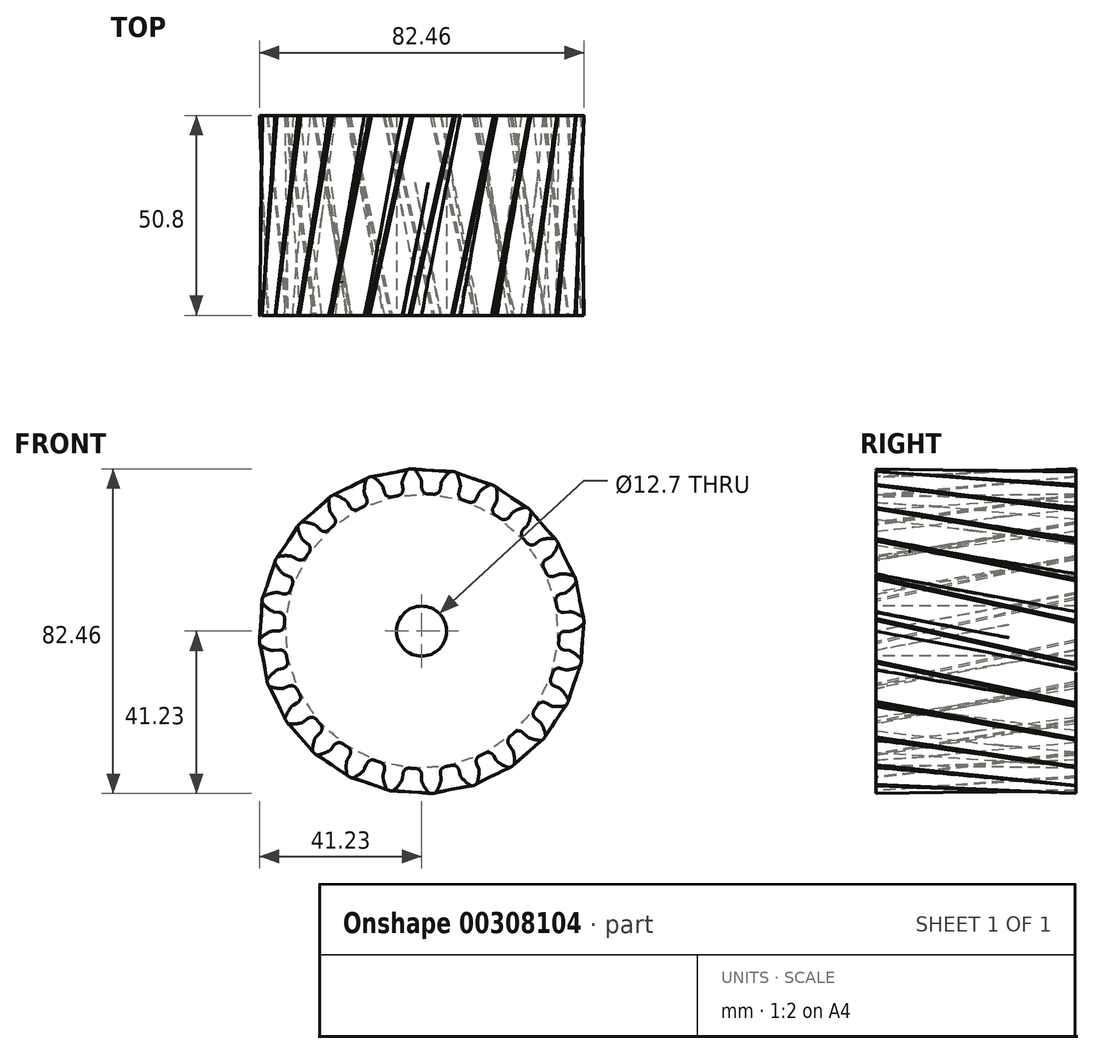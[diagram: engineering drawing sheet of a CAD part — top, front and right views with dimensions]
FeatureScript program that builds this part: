
annotation { "Feature Type Name" : "Feature", "Feature Type Description" : "" }
export const myFeature = defineFeature(function(context is Context, id is Id, definition is map)
    precondition{}
    {
        {
            var Q0;
            Q0=qCreatedBy(makeId("Front.planeOp"),FACE);
            var sketch = newSketch(context, id + "F0", { "sketchPlane" : qUnion([Q0])});
            skArc(sketch, "E0", {"start": v(-6.07, 34.4) * mm, "mid": v(-6.81, 34.25) * mm, "end": v(-7.56, 34.1) * mm});
            skArc(sketch, "E1.trimOffspring", {"start": v(-0.12, 38.41) * mm, "mid": v(-0.85, 39.8) * mm, "end": v(-1.8, 41.06) * mm});
            skLineSegment(sketch, "E2", {"start": v(-2.18, 41.23) * mm, "end": v(-2.7, 41.23) * mm});
            skLineSegment(sketch, "E3", {"start": v(0, 37.8) * mm, "end": v(0, 36.48) * mm});
            skLineSegment(sketch, "E4.MirrorCS", {"start": v(-3.22, 41.16) * mm, "end": v(-2.7, 41.23) * mm});
            skArc(sketch, "E5.MirrorCS", {"start": v(-4.9, 38.1) * mm, "mid": v(-4.35, 39.58) * mm, "end": v(-3.57, 40.95) * mm});
            skLineSegment(sketch, "E6.MirrorCS", {"start": v(-4.94, 37.47) * mm, "end": v(-4.77, 36.16) * mm});
            skPoint(sketch, "E7.visualSharp", {"position": v(-3.44, 41.13) * mm});
            skArc(sketch, "E7.filletArc", {"start": v(-3.22, 41.16) * mm, "mid": v(-3.41, 41.1) * mm, "end": v(-3.57, 40.95) * mm});
            skPoint(sketch, "E8.visualSharp", {"position": v(-1.96, 41.23) * mm});
            skArc(sketch, "E8.filletArc", {"start": v(-1.8, 41.06) * mm, "mid": v(-1.98, 41.18) * mm, "end": v(-2.18, 41.23) * mm});
            skPoint(sketch, "E9.visualSharp", {"position": v(-4.98, 37.77) * mm});
            skArc(sketch, "E9.filletArc", {"start": v(-4.9, 38.1) * mm, "mid": v(-4.95, 37.79) * mm, "end": v(-4.94, 37.47) * mm});
            skPoint(sketch, "E10.visualSharp", {"position": v(0, 38.1) * mm});
            skArc(sketch, "E10.filletArc", {"start": v(0, 37.8) * mm, "mid": v(-0.02, 38.1) * mm, "end": v(-0.12, 38.41) * mm});
            skPoint(sketch, "E11.visualSharp", {"position": v(0, 34.92) * mm});
            skArc(sketch, "E11.filletArc", {"start": v(0, 36.48) * mm, "mid": v(0.45, 35.38) * mm, "end": v(1.53, 34.9) * mm});
            skPoint(sketch, "E12.visualSharp", {"position": v(-4.57, 34.63) * mm});
            skArc(sketch, "E12.filletArc", {"start": v(-6.07, 34.4) * mm, "mid": v(-5.06, 35.02) * mm, "end": v(-4.77, 36.16) * mm});
            skLineSegment(sketch, "E13.1.0", {"start": v(-14.47, 34.91) * mm, "end": v(-13.97, 33.7) * mm});
            skArc(sketch, "E13.1.1", {"start": v(-14.76, 31.65) * mm, "mid": v(-13.95, 32.51) * mm, "end": v(-13.97, 33.7) * mm});
            skLineSegment(sketch, "E13.1.2", {"start": v(-9.77, 36.5) * mm, "end": v(-9.43, 35.24) * mm});
            skArc(sketch, "E13.1.3", {"start": v(-9.43, 35.24) * mm, "mid": v(-8.72, 34.3) * mm, "end": v(-7.56, 34.1) * mm});
            skArc(sketch, "E13.1.4", {"start": v(-14.6, 35.53) * mm, "mid": v(-14.56, 35.22) * mm, "end": v(-14.47, 34.91) * mm});
            skArc(sketch, "E13.1.5", {"start": v(-14.6, 35.53) * mm, "mid": v(-14.45, 37.1) * mm, "end": v(-14.04, 38.63) * mm});
            skArc(sketch, "E13.1.6", {"start": v(-13.76, 38.93) * mm, "mid": v(-13.93, 38.8) * mm, "end": v(-14.04, 38.63) * mm});
            skLineSegment(sketch, "E13.1.7", {"start": v(-13.76, 38.93) * mm, "end": v(-13.28, 39.12) * mm});
            skLineSegment(sketch, "E13.1.8", {"start": v(-12.78, 39.26) * mm, "end": v(-13.28, 39.12) * mm});
            skArc(sketch, "E13.1.9", {"start": v(-12.37, 39.2) * mm, "mid": v(-12.57, 39.27) * mm, "end": v(-12.78, 39.26) * mm});
            skArc(sketch, "E13.1.10", {"start": v(-10.06, 37.07) * mm, "mid": v(-11.13, 38.23) * mm, "end": v(-12.37, 39.2) * mm});
            skArc(sketch, "E13.1.11", {"start": v(-9.77, 36.5) * mm, "mid": v(-9.89, 36.8) * mm, "end": v(-10.06, 37.07) * mm});
            skLineSegment(sketch, "E13.2.0", {"start": v(-23.01, 29.98) * mm, "end": v(-22.21, 28.93) * mm});
            skArc(sketch, "E13.2.1", {"start": v(-22.45, 26.75) * mm, "mid": v(-21.9, 27.8) * mm, "end": v(-22.21, 28.93) * mm});
            skLineSegment(sketch, "E13.2.2", {"start": v(-18.89, 32.73) * mm, "end": v(-18.23, 31.6) * mm});
            skArc(sketch, "E13.2.3", {"start": v(-18.23, 31.6) * mm, "mid": v(-17.3, 30.86) * mm, "end": v(-16.12, 30.98) * mm});
            skArc(sketch, "E13.2.4", {"start": v(-23.3, 30.55) * mm, "mid": v(-23.18, 30.25) * mm, "end": v(-23.01, 29.98) * mm});
            skArc(sketch, "E13.2.5", {"start": v(-23.3, 30.55) * mm, "mid": v(-23.56, 32.1) * mm, "end": v(-23.56, 33.68) * mm});
            skArc(sketch, "E13.2.6", {"start": v(-23.36, 34.04) * mm, "mid": v(-23.5, 33.88) * mm, "end": v(-23.56, 33.68) * mm});
            skLineSegment(sketch, "E13.2.7", {"start": v(-23.36, 34.04) * mm, "end": v(-22.95, 34.35) * mm});
            skLineSegment(sketch, "E13.2.8", {"start": v(-22.5, 34.61) * mm, "end": v(-22.95, 34.35) * mm});
            skArc(sketch, "E13.2.9", {"start": v(-22.1, 34.66) * mm, "mid": v(-22.3, 34.68) * mm, "end": v(-22.5, 34.61) * mm});
            skArc(sketch, "E13.2.10", {"start": v(-19.3, 33.2) * mm, "mid": v(-20.64, 34.05) * mm, "end": v(-22.1, 34.66) * mm});
            skArc(sketch, "E13.2.11", {"start": v(-18.89, 32.73) * mm, "mid": v(-19.07, 33) * mm, "end": v(-19.3, 33.2) * mm});
            skLineSegment(sketch, "E14.2.3.0", {"start": v(-29.99, 23) * mm, "end": v(-28.94, 22.2) * mm});
            skArc(sketch, "E14.3.3.0", {"start": v(-28.61, 20.03) * mm, "mid": v(-28.34, 21.18) * mm, "end": v(-28.94, 22.2) * mm});
            skLineSegment(sketch, "E14.7.3.0", {"start": v(-26.72, 26.73) * mm, "end": v(-25.79, 25.8) * mm});
            skArc(sketch, "E14.10.3.0", {"start": v(-25.79, 25.8) * mm, "mid": v(-24.7, 25.34) * mm, "end": v(-23.6, 25.75) * mm});
            skArc(sketch, "E14.14.3.0", {"start": v(-30.4, 23.48) * mm, "mid": v(-30.22, 23.22) * mm, "end": v(-29.99, 23) * mm});
            skArc(sketch, "E14.18.3.0", {"start": v(-30.4, 23.48) * mm, "mid": v(-31.06, 24.9) * mm, "end": v(-31.48, 26.43) * mm});
            skArc(sketch, "E14.22.3.0", {"start": v(-31.38, 26.83) * mm, "mid": v(-31.47, 26.64) * mm, "end": v(-31.48, 26.43) * mm});
            skLineSegment(sketch, "E14.26.3.0", {"start": v(-31.38, 26.83) * mm, "end": v(-31.06, 27.24) * mm});
            skLineSegment(sketch, "E14.29.3.0", {"start": v(-30.7, 27.6) * mm, "end": v(-31.06, 27.24) * mm});
            skArc(sketch, "E14.32.3.0", {"start": v(-30.31, 27.76) * mm, "mid": v(-30.52, 27.72) * mm, "end": v(-30.7, 27.6) * mm});
            skArc(sketch, "E14.36.3.0", {"start": v(-27.25, 27.08) * mm, "mid": v(-28.75, 27.54) * mm, "end": v(-30.31, 27.76) * mm});
            skArc(sketch, "E14.40.3.0", {"start": v(-26.72, 26.73) * mm, "mid": v(-26.96, 26.93) * mm, "end": v(-27.25, 27.08) * mm});
            skLineSegment(sketch, "E14.2.4.0", {"start": v(-34.92, 14.45) * mm, "end": v(-33.7, 13.95) * mm});
            skArc(sketch, "E14.3.4.0", {"start": v(-32.82, 11.94) * mm, "mid": v(-32.86, 13.12) * mm, "end": v(-33.7, 13.95) * mm});
            skLineSegment(sketch, "E14.7.4.0", {"start": v(-32.72, 18.9) * mm, "end": v(-31.59, 18.25) * mm});
            skArc(sketch, "E14.10.4.0", {"start": v(-31.59, 18.25) * mm, "mid": v(-30.42, 18.08) * mm, "end": v(-29.45, 18.77) * mm});
            skArc(sketch, "E14.14.4.0", {"start": v(-35.44, 14.8) * mm, "mid": v(-35.2, 14.6) * mm, "end": v(-34.92, 14.45) * mm});
            skArc(sketch, "E14.18.4.0", {"start": v(-35.44, 14.8) * mm, "mid": v(-36.45, 16.02) * mm, "end": v(-37.24, 17.38) * mm});
            skArc(sketch, "E14.22.4.0", {"start": v(-37.25, 17.8) * mm, "mid": v(-37.3, 17.59) * mm, "end": v(-37.24, 17.38) * mm});
            skLineSegment(sketch, "E14.26.4.0", {"start": v(-37.25, 17.8) * mm, "end": v(-37.06, 18.27) * mm});
            skLineSegment(sketch, "E14.29.4.0", {"start": v(-36.8, 18.72) * mm, "end": v(-37.06, 18.27) * mm});
            skArc(sketch, "E14.32.4.0", {"start": v(-36.46, 18.96) * mm, "mid": v(-36.66, 18.88) * mm, "end": v(-36.8, 18.72) * mm});
            skArc(sketch, "E14.36.4.0", {"start": v(-33.33, 19.1) * mm, "mid": v(-34.9, 19.16) * mm, "end": v(-36.46, 18.96) * mm});
            skArc(sketch, "E14.40.4.0", {"start": v(-32.72, 18.9) * mm, "mid": v(-33.01, 19.03) * mm, "end": v(-33.33, 19.1) * mm});
            skLineSegment(sketch, "E14.2.5.0", {"start": v(-37.47, 4.92) * mm, "end": v(-36.17, 4.75) * mm});
            skArc(sketch, "E14.3.5.0", {"start": v(-34.8, 3.04) * mm, "mid": v(-35.14, 4.17) * mm, "end": v(-36.17, 4.75) * mm});
            skLineSegment(sketch, "E14.7.5.0", {"start": v(-36.5, 9.79) * mm, "end": v(-35.23, 9.45) * mm});
            skArc(sketch, "E14.10.5.0", {"start": v(-35.23, 9.45) * mm, "mid": v(-34.06, 9.6) * mm, "end": v(-33.3, 10.5) * mm});
            skArc(sketch, "E14.14.5.0", {"start": v(-38.07, 5.13) * mm, "mid": v(-37.78, 5) * mm, "end": v(-37.47, 4.92) * mm});
            skArc(sketch, "E14.18.5.0", {"start": v(-38.07, 5.13) * mm, "mid": v(-39.36, 6.04) * mm, "end": v(-40.47, 7.15) * mm});
            skArc(sketch, "E14.22.5.0", {"start": v(-40.6, 7.55) * mm, "mid": v(-40.57, 7.34) * mm, "end": v(-40.47, 7.15) * mm});
            skLineSegment(sketch, "E14.26.5.0", {"start": v(-40.6, 7.55) * mm, "end": v(-40.52, 8.06) * mm});
            skLineSegment(sketch, "E14.29.5.0", {"start": v(-40.39, 8.56) * mm, "end": v(-40.52, 8.06) * mm});
            skArc(sketch, "E14.32.5.0", {"start": v(-40.13, 8.88) * mm, "mid": v(-40.3, 8.75) * mm, "end": v(-40.39, 8.56) * mm});
            skArc(sketch, "E14.36.5.0", {"start": v(-37.13, 9.83) * mm, "mid": v(-38.67, 9.48) * mm, "end": v(-40.13, 8.88) * mm});
            skArc(sketch, "E14.40.5.0", {"start": v(-36.5, 9.79) * mm, "mid": v(-36.82, 9.84) * mm, "end": v(-37.13, 9.83) * mm});
            skLineSegment(sketch, "E14.2.6.0", {"start": v(-37.47, -4.94) * mm, "end": v(-36.16, -4.77) * mm});
            skArc(sketch, "E14.3.6.0", {"start": v(-34.4, -6.07) * mm, "mid": v(-35.02, -5.06) * mm, "end": v(-36.16, -4.77) * mm});
            skLineSegment(sketch, "E14.7.6.0", {"start": v(-37.8, 0) * mm, "end": v(-36.48, 0) * mm});
            skArc(sketch, "E14.10.6.0", {"start": v(-36.48, 0) * mm, "mid": v(-35.38, 0.45) * mm, "end": v(-34.9, 1.53) * mm});
            skArc(sketch, "E14.14.6.0", {"start": v(-38.1, -4.9) * mm, "mid": v(-37.79, -4.95) * mm, "end": v(-37.47, -4.94) * mm});
            skArc(sketch, "E14.18.6.0", {"start": v(-38.1, -4.9) * mm, "mid": v(-39.58, -4.35) * mm, "end": v(-40.95, -3.57) * mm});
            skArc(sketch, "E14.22.6.0", {"start": v(-41.16, -3.22) * mm, "mid": v(-41.1, -3.41) * mm, "end": v(-40.95, -3.57) * mm});
            skLineSegment(sketch, "E14.26.6.0", {"start": v(-41.16, -3.22) * mm, "end": v(-41.23, -2.7) * mm});
            skLineSegment(sketch, "E14.29.6.0", {"start": v(-41.23, -2.18) * mm, "end": v(-41.23, -2.7) * mm});
            skArc(sketch, "E14.32.6.0", {"start": v(-41.06, -1.8) * mm, "mid": v(-41.18, -1.98) * mm, "end": v(-41.23, -2.18) * mm});
            skArc(sketch, "E14.36.6.0", {"start": v(-38.41, -0.12) * mm, "mid": v(-39.8, -0.85) * mm, "end": v(-41.06, -1.8) * mm});
            skArc(sketch, "E14.40.6.0", {"start": v(-37.8, 0) * mm, "mid": v(-38.1, -0.02) * mm, "end": v(-38.41, -0.12) * mm});
            skLineSegment(sketch, "E14.2.7.0", {"start": v(-34.91, -14.47) * mm, "end": v(-33.7, -13.97) * mm});
            skArc(sketch, "E14.3.7.0", {"start": v(-31.65, -14.76) * mm, "mid": v(-32.51, -13.95) * mm, "end": v(-33.7, -13.97) * mm});
            skLineSegment(sketch, "E14.7.7.0", {"start": v(-36.5, -9.77) * mm, "end": v(-35.24, -9.43) * mm});
            skArc(sketch, "E14.10.7.0", {"start": v(-35.24, -9.43) * mm, "mid": v(-34.3, -8.72) * mm, "end": v(-34.1, -7.56) * mm});
            skArc(sketch, "E14.14.7.0", {"start": v(-35.53, -14.6) * mm, "mid": v(-35.22, -14.56) * mm, "end": v(-34.91, -14.47) * mm});
            skArc(sketch, "E14.18.7.0", {"start": v(-35.53, -14.6) * mm, "mid": v(-37.1, -14.45) * mm, "end": v(-38.63, -14.04) * mm});
            skArc(sketch, "E14.22.7.0", {"start": v(-38.93, -13.76) * mm, "mid": v(-38.8, -13.93) * mm, "end": v(-38.63, -14.04) * mm});
            skLineSegment(sketch, "E14.26.7.0", {"start": v(-38.93, -13.76) * mm, "end": v(-39.12, -13.28) * mm});
            skLineSegment(sketch, "E14.29.7.0", {"start": v(-39.26, -12.78) * mm, "end": v(-39.12, -13.28) * mm});
            skArc(sketch, "E14.32.7.0", {"start": v(-39.2, -12.37) * mm, "mid": v(-39.27, -12.57) * mm, "end": v(-39.26, -12.78) * mm});
            skArc(sketch, "E14.36.7.0", {"start": v(-37.07, -10.06) * mm, "mid": v(-38.23, -11.13) * mm, "end": v(-39.2, -12.37) * mm});
            skArc(sketch, "E14.40.7.0", {"start": v(-36.5, -9.77) * mm, "mid": v(-36.8, -9.89) * mm, "end": v(-37.07, -10.06) * mm});
            skLineSegment(sketch, "E14.2.8.0", {"start": v(-29.98, -23.01) * mm, "end": v(-28.93, -22.21) * mm});
            skArc(sketch, "E14.3.8.0", {"start": v(-26.75, -22.45) * mm, "mid": v(-27.8, -21.9) * mm, "end": v(-28.93, -22.21) * mm});
            skLineSegment(sketch, "E14.7.8.0", {"start": v(-32.73, -18.89) * mm, "end": v(-31.6, -18.23) * mm});
            skArc(sketch, "E14.10.8.0", {"start": v(-31.6, -18.23) * mm, "mid": v(-30.86, -17.3) * mm, "end": v(-30.98, -16.12) * mm});
            skArc(sketch, "E14.14.8.0", {"start": v(-30.55, -23.3) * mm, "mid": v(-30.25, -23.18) * mm, "end": v(-29.98, -23.01) * mm});
            skArc(sketch, "E14.18.8.0", {"start": v(-30.55, -23.3) * mm, "mid": v(-32.1, -23.56) * mm, "end": v(-33.68, -23.56) * mm});
            skArc(sketch, "E14.22.8.0", {"start": v(-34.04, -23.36) * mm, "mid": v(-33.88, -23.5) * mm, "end": v(-33.68, -23.56) * mm});
            skLineSegment(sketch, "E14.26.8.0", {"start": v(-34.04, -23.36) * mm, "end": v(-34.35, -22.95) * mm});
            skLineSegment(sketch, "E14.29.8.0", {"start": v(-34.61, -22.5) * mm, "end": v(-34.35, -22.95) * mm});
            skArc(sketch, "E14.32.8.0", {"start": v(-34.66, -22.1) * mm, "mid": v(-34.68, -22.3) * mm, "end": v(-34.61, -22.5) * mm});
            skArc(sketch, "E14.36.8.0", {"start": v(-33.2, -19.3) * mm, "mid": v(-34.05, -20.64) * mm, "end": v(-34.66, -22.1) * mm});
            skArc(sketch, "E14.40.8.0", {"start": v(-32.73, -18.89) * mm, "mid": v(-33, -19.07) * mm, "end": v(-33.2, -19.3) * mm});
            skLineSegment(sketch, "E14.2.9.0", {"start": v(-23, -29.99) * mm, "end": v(-22.2, -28.94) * mm});
            skArc(sketch, "E14.3.9.0", {"start": v(-20.03, -28.61) * mm, "mid": v(-21.18, -28.34) * mm, "end": v(-22.2, -28.94) * mm});
            skLineSegment(sketch, "E14.7.9.0", {"start": v(-26.73, -26.72) * mm, "end": v(-25.8, -25.79) * mm});
            skArc(sketch, "E14.10.9.0", {"start": v(-25.8, -25.79) * mm, "mid": v(-25.34, -24.7) * mm, "end": v(-25.75, -23.6) * mm});
            skArc(sketch, "E14.14.9.0", {"start": v(-23.48, -30.4) * mm, "mid": v(-23.22, -30.22) * mm, "end": v(-23, -29.99) * mm});
            skArc(sketch, "E14.18.9.0", {"start": v(-23.48, -30.4) * mm, "mid": v(-24.9, -31.06) * mm, "end": v(-26.43, -31.48) * mm});
            skArc(sketch, "E14.22.9.0", {"start": v(-26.83, -31.38) * mm, "mid": v(-26.64, -31.47) * mm, "end": v(-26.43, -31.48) * mm});
            skLineSegment(sketch, "E14.26.9.0", {"start": v(-26.83, -31.38) * mm, "end": v(-27.24, -31.06) * mm});
            skLineSegment(sketch, "E14.29.9.0", {"start": v(-27.6, -30.7) * mm, "end": v(-27.24, -31.06) * mm});
            skArc(sketch, "E14.32.9.0", {"start": v(-27.76, -30.31) * mm, "mid": v(-27.72, -30.52) * mm, "end": v(-27.6, -30.7) * mm});
            skArc(sketch, "E14.36.9.0", {"start": v(-27.08, -27.25) * mm, "mid": v(-27.54, -28.75) * mm, "end": v(-27.76, -30.31) * mm});
            skArc(sketch, "E14.40.9.0", {"start": v(-26.73, -26.72) * mm, "mid": v(-26.93, -26.96) * mm, "end": v(-27.08, -27.25) * mm});
            skLineSegment(sketch, "E14.2.10.0", {"start": v(-14.45, -34.92) * mm, "end": v(-13.95, -33.7) * mm});
            skArc(sketch, "E14.3.10.0", {"start": v(-11.94, -32.82) * mm, "mid": v(-13.12, -32.86) * mm, "end": v(-13.95, -33.7) * mm});
            skLineSegment(sketch, "E14.7.10.0", {"start": v(-18.9, -32.72) * mm, "end": v(-18.25, -31.59) * mm});
            skArc(sketch, "E14.10.10.0", {"start": v(-18.25, -31.59) * mm, "mid": v(-18.08, -30.42) * mm, "end": v(-18.77, -29.45) * mm});
            skArc(sketch, "E14.14.10.0", {"start": v(-14.8, -35.44) * mm, "mid": v(-14.6, -35.2) * mm, "end": v(-14.45, -34.92) * mm});
            skArc(sketch, "E14.18.10.0", {"start": v(-14.8, -35.44) * mm, "mid": v(-16.02, -36.45) * mm, "end": v(-17.38, -37.24) * mm});
            skArc(sketch, "E14.22.10.0", {"start": v(-17.8, -37.25) * mm, "mid": v(-17.59, -37.3) * mm, "end": v(-17.38, -37.24) * mm});
            skLineSegment(sketch, "E14.26.10.0", {"start": v(-17.8, -37.25) * mm, "end": v(-18.27, -37.06) * mm});
            skLineSegment(sketch, "E14.29.10.0", {"start": v(-18.72, -36.8) * mm, "end": v(-18.27, -37.06) * mm});
            skArc(sketch, "E14.32.10.0", {"start": v(-18.96, -36.46) * mm, "mid": v(-18.88, -36.66) * mm, "end": v(-18.72, -36.8) * mm});
            skArc(sketch, "E14.36.10.0", {"start": v(-19.1, -33.33) * mm, "mid": v(-19.16, -34.9) * mm, "end": v(-18.96, -36.46) * mm});
            skArc(sketch, "E14.40.10.0", {"start": v(-18.9, -32.72) * mm, "mid": v(-19.03, -33.01) * mm, "end": v(-19.1, -33.33) * mm});
            skLineSegment(sketch, "E14.2.11.0", {"start": v(-4.92, -37.47) * mm, "end": v(-4.75, -36.17) * mm});
            skArc(sketch, "E14.3.11.0", {"start": v(-3.04, -34.8) * mm, "mid": v(-4.17, -35.14) * mm, "end": v(-4.75, -36.17) * mm});
            skLineSegment(sketch, "E14.7.11.0", {"start": v(-9.79, -36.5) * mm, "end": v(-9.45, -35.23) * mm});
            skArc(sketch, "E14.10.11.0", {"start": v(-9.45, -35.23) * mm, "mid": v(-9.6, -34.06) * mm, "end": v(-10.5, -33.3) * mm});
            skArc(sketch, "E14.14.11.0", {"start": v(-5.13, -38.07) * mm, "mid": v(-5, -37.78) * mm, "end": v(-4.92, -37.47) * mm});
            skArc(sketch, "E14.18.11.0", {"start": v(-5.13, -38.07) * mm, "mid": v(-6.04, -39.36) * mm, "end": v(-7.15, -40.47) * mm});
            skArc(sketch, "E14.22.11.0", {"start": v(-7.55, -40.6) * mm, "mid": v(-7.34, -40.57) * mm, "end": v(-7.15, -40.47) * mm});
            skLineSegment(sketch, "E14.26.11.0", {"start": v(-7.55, -40.6) * mm, "end": v(-8.06, -40.52) * mm});
            skLineSegment(sketch, "E14.29.11.0", {"start": v(-8.56, -40.39) * mm, "end": v(-8.06, -40.52) * mm});
            skArc(sketch, "E14.32.11.0", {"start": v(-8.88, -40.13) * mm, "mid": v(-8.75, -40.3) * mm, "end": v(-8.56, -40.39) * mm});
            skArc(sketch, "E14.36.11.0", {"start": v(-9.83, -37.13) * mm, "mid": v(-9.48, -38.67) * mm, "end": v(-8.88, -40.13) * mm});
            skArc(sketch, "E14.40.11.0", {"start": v(-9.79, -36.5) * mm, "mid": v(-9.84, -36.82) * mm, "end": v(-9.83, -37.13) * mm});
            skLineSegment(sketch, "E14.2.12.0", {"start": v(4.94, -37.47) * mm, "end": v(4.77, -36.16) * mm});
            skArc(sketch, "E14.3.12.0", {"start": v(6.07, -34.4) * mm, "mid": v(5.06, -35.02) * mm, "end": v(4.77, -36.16) * mm});
            skLineSegment(sketch, "E14.7.12.0", {"start": v(0, -37.8) * mm, "end": v(0, -36.48) * mm});
            skArc(sketch, "E14.10.12.0", {"start": v(0, -36.48) * mm, "mid": v(-0.45, -35.38) * mm, "end": v(-1.53, -34.9) * mm});
            skArc(sketch, "E14.14.12.0", {"start": v(4.9, -38.1) * mm, "mid": v(4.95, -37.79) * mm, "end": v(4.94, -37.47) * mm});
            skArc(sketch, "E14.18.12.0", {"start": v(4.9, -38.1) * mm, "mid": v(4.35, -39.58) * mm, "end": v(3.57, -40.95) * mm});
            skArc(sketch, "E14.22.12.0", {"start": v(3.22, -41.16) * mm, "mid": v(3.41, -41.1) * mm, "end": v(3.57, -40.95) * mm});
            skLineSegment(sketch, "E14.26.12.0", {"start": v(3.22, -41.16) * mm, "end": v(2.7, -41.23) * mm});
            skLineSegment(sketch, "E14.29.12.0", {"start": v(2.18, -41.23) * mm, "end": v(2.7, -41.23) * mm});
            skArc(sketch, "E14.32.12.0", {"start": v(1.8, -41.06) * mm, "mid": v(1.98, -41.18) * mm, "end": v(2.18, -41.23) * mm});
            skArc(sketch, "E14.36.12.0", {"start": v(0.12, -38.41) * mm, "mid": v(0.85, -39.8) * mm, "end": v(1.8, -41.06) * mm});
            skArc(sketch, "E14.40.12.0", {"start": v(0, -37.8) * mm, "mid": v(0.02, -38.1) * mm, "end": v(0.12, -38.41) * mm});
            skLineSegment(sketch, "E14.2.13.0", {"start": v(14.47, -34.91) * mm, "end": v(13.97, -33.7) * mm});
            skArc(sketch, "E14.3.13.0", {"start": v(14.76, -31.65) * mm, "mid": v(13.95, -32.51) * mm, "end": v(13.97, -33.7) * mm});
            skLineSegment(sketch, "E14.7.13.0", {"start": v(9.77, -36.5) * mm, "end": v(9.43, -35.24) * mm});
            skArc(sketch, "E14.10.13.0", {"start": v(9.43, -35.24) * mm, "mid": v(8.72, -34.3) * mm, "end": v(7.56, -34.1) * mm});
            skArc(sketch, "E14.14.13.0", {"start": v(14.6, -35.53) * mm, "mid": v(14.56, -35.22) * mm, "end": v(14.47, -34.91) * mm});
            skArc(sketch, "E14.18.13.0", {"start": v(14.6, -35.53) * mm, "mid": v(14.45, -37.1) * mm, "end": v(14.04, -38.63) * mm});
            skArc(sketch, "E14.22.13.0", {"start": v(13.76, -38.93) * mm, "mid": v(13.93, -38.8) * mm, "end": v(14.04, -38.63) * mm});
            skLineSegment(sketch, "E14.26.13.0", {"start": v(13.76, -38.93) * mm, "end": v(13.28, -39.12) * mm});
            skLineSegment(sketch, "E14.29.13.0", {"start": v(12.78, -39.26) * mm, "end": v(13.28, -39.12) * mm});
            skArc(sketch, "E14.32.13.0", {"start": v(12.37, -39.2) * mm, "mid": v(12.57, -39.27) * mm, "end": v(12.78, -39.26) * mm});
            skArc(sketch, "E14.36.13.0", {"start": v(10.06, -37.07) * mm, "mid": v(11.13, -38.23) * mm, "end": v(12.37, -39.2) * mm});
            skArc(sketch, "E14.40.13.0", {"start": v(9.77, -36.5) * mm, "mid": v(9.89, -36.8) * mm, "end": v(10.06, -37.07) * mm});
            skLineSegment(sketch, "E14.2.14.0", {"start": v(23.01, -29.98) * mm, "end": v(22.21, -28.93) * mm});
            skArc(sketch, "E14.3.14.0", {"start": v(22.45, -26.75) * mm, "mid": v(21.9, -27.8) * mm, "end": v(22.21, -28.93) * mm});
            skLineSegment(sketch, "E14.7.14.0", {"start": v(18.89, -32.73) * mm, "end": v(18.23, -31.6) * mm});
            skArc(sketch, "E14.10.14.0", {"start": v(18.23, -31.6) * mm, "mid": v(17.3, -30.86) * mm, "end": v(16.12, -30.98) * mm});
            skArc(sketch, "E14.14.14.0", {"start": v(23.3, -30.55) * mm, "mid": v(23.18, -30.25) * mm, "end": v(23.01, -29.98) * mm});
            skArc(sketch, "E14.18.14.0", {"start": v(23.3, -30.55) * mm, "mid": v(23.56, -32.1) * mm, "end": v(23.56, -33.68) * mm});
            skArc(sketch, "E14.22.14.0", {"start": v(23.36, -34.04) * mm, "mid": v(23.5, -33.88) * mm, "end": v(23.56, -33.68) * mm});
            skLineSegment(sketch, "E14.26.14.0", {"start": v(23.36, -34.04) * mm, "end": v(22.95, -34.35) * mm});
            skLineSegment(sketch, "E14.29.14.0", {"start": v(22.5, -34.61) * mm, "end": v(22.95, -34.35) * mm});
            skArc(sketch, "E14.32.14.0", {"start": v(22.1, -34.66) * mm, "mid": v(22.3, -34.68) * mm, "end": v(22.5, -34.61) * mm});
            skArc(sketch, "E14.36.14.0", {"start": v(19.3, -33.2) * mm, "mid": v(20.64, -34.05) * mm, "end": v(22.1, -34.66) * mm});
            skArc(sketch, "E14.40.14.0", {"start": v(18.89, -32.73) * mm, "mid": v(19.07, -33) * mm, "end": v(19.3, -33.2) * mm});
            skLineSegment(sketch, "E14.2.15.0", {"start": v(29.99, -23) * mm, "end": v(28.94, -22.2) * mm});
            skArc(sketch, "E14.3.15.0", {"start": v(28.61, -20.03) * mm, "mid": v(28.34, -21.18) * mm, "end": v(28.94, -22.2) * mm});
            skLineSegment(sketch, "E14.7.15.0", {"start": v(26.72, -26.73) * mm, "end": v(25.79, -25.8) * mm});
            skArc(sketch, "E14.10.15.0", {"start": v(25.79, -25.8) * mm, "mid": v(24.7, -25.34) * mm, "end": v(23.6, -25.75) * mm});
            skArc(sketch, "E14.14.15.0", {"start": v(30.4, -23.48) * mm, "mid": v(30.22, -23.22) * mm, "end": v(29.99, -23) * mm});
            skArc(sketch, "E14.18.15.0", {"start": v(30.4, -23.48) * mm, "mid": v(31.06, -24.9) * mm, "end": v(31.48, -26.43) * mm});
            skArc(sketch, "E14.22.15.0", {"start": v(31.38, -26.83) * mm, "mid": v(31.47, -26.64) * mm, "end": v(31.48, -26.43) * mm});
            skLineSegment(sketch, "E14.26.15.0", {"start": v(31.38, -26.83) * mm, "end": v(31.06, -27.24) * mm});
            skLineSegment(sketch, "E14.29.15.0", {"start": v(30.7, -27.6) * mm, "end": v(31.06, -27.24) * mm});
            skArc(sketch, "E14.32.15.0", {"start": v(30.31, -27.76) * mm, "mid": v(30.52, -27.72) * mm, "end": v(30.7, -27.6) * mm});
            skArc(sketch, "E14.36.15.0", {"start": v(27.25, -27.08) * mm, "mid": v(28.75, -27.54) * mm, "end": v(30.31, -27.76) * mm});
            skArc(sketch, "E14.40.15.0", {"start": v(26.72, -26.73) * mm, "mid": v(26.96, -26.93) * mm, "end": v(27.25, -27.08) * mm});
            skLineSegment(sketch, "E14.2.16.0", {"start": v(34.92, -14.45) * mm, "end": v(33.7, -13.95) * mm});
            skArc(sketch, "E14.3.16.0", {"start": v(32.82, -11.94) * mm, "mid": v(32.86, -13.12) * mm, "end": v(33.7, -13.95) * mm});
            skLineSegment(sketch, "E14.7.16.0", {"start": v(32.72, -18.9) * mm, "end": v(31.59, -18.25) * mm});
            skArc(sketch, "E14.10.16.0", {"start": v(31.59, -18.25) * mm, "mid": v(30.42, -18.08) * mm, "end": v(29.45, -18.77) * mm});
            skArc(sketch, "E14.14.16.0", {"start": v(35.44, -14.8) * mm, "mid": v(35.2, -14.6) * mm, "end": v(34.92, -14.45) * mm});
            skArc(sketch, "E14.18.16.0", {"start": v(35.44, -14.8) * mm, "mid": v(36.45, -16.02) * mm, "end": v(37.24, -17.38) * mm});
            skArc(sketch, "E14.22.16.0", {"start": v(37.25, -17.8) * mm, "mid": v(37.3, -17.59) * mm, "end": v(37.24, -17.38) * mm});
            skLineSegment(sketch, "E14.26.16.0", {"start": v(37.25, -17.8) * mm, "end": v(37.06, -18.27) * mm});
            skLineSegment(sketch, "E14.29.16.0", {"start": v(36.8, -18.72) * mm, "end": v(37.06, -18.27) * mm});
            skArc(sketch, "E14.32.16.0", {"start": v(36.46, -18.96) * mm, "mid": v(36.66, -18.88) * mm, "end": v(36.8, -18.72) * mm});
            skArc(sketch, "E14.36.16.0", {"start": v(33.33, -19.1) * mm, "mid": v(34.9, -19.16) * mm, "end": v(36.46, -18.96) * mm});
            skArc(sketch, "E14.40.16.0", {"start": v(32.72, -18.9) * mm, "mid": v(33.01, -19.03) * mm, "end": v(33.33, -19.1) * mm});
            skLineSegment(sketch, "E14.2.17.0", {"start": v(37.47, -4.92) * mm, "end": v(36.17, -4.75) * mm});
            skArc(sketch, "E14.3.17.0", {"start": v(34.8, -3.04) * mm, "mid": v(35.14, -4.17) * mm, "end": v(36.17, -4.75) * mm});
            skLineSegment(sketch, "E14.7.17.0", {"start": v(36.5, -9.79) * mm, "end": v(35.23, -9.45) * mm});
            skArc(sketch, "E14.10.17.0", {"start": v(35.23, -9.45) * mm, "mid": v(34.06, -9.6) * mm, "end": v(33.3, -10.5) * mm});
            skArc(sketch, "E14.14.17.0", {"start": v(38.07, -5.13) * mm, "mid": v(37.78, -5) * mm, "end": v(37.47, -4.92) * mm});
            skArc(sketch, "E14.18.17.0", {"start": v(38.07, -5.13) * mm, "mid": v(39.36, -6.04) * mm, "end": v(40.47, -7.15) * mm});
            skArc(sketch, "E14.22.17.0", {"start": v(40.6, -7.55) * mm, "mid": v(40.57, -7.34) * mm, "end": v(40.47, -7.15) * mm});
            skLineSegment(sketch, "E14.26.17.0", {"start": v(40.6, -7.55) * mm, "end": v(40.52, -8.06) * mm});
            skLineSegment(sketch, "E14.29.17.0", {"start": v(40.39, -8.56) * mm, "end": v(40.52, -8.06) * mm});
            skArc(sketch, "E14.32.17.0", {"start": v(40.13, -8.88) * mm, "mid": v(40.3, -8.75) * mm, "end": v(40.39, -8.56) * mm});
            skArc(sketch, "E14.36.17.0", {"start": v(37.13, -9.83) * mm, "mid": v(38.67, -9.48) * mm, "end": v(40.13, -8.88) * mm});
            skArc(sketch, "E14.40.17.0", {"start": v(36.5, -9.79) * mm, "mid": v(36.82, -9.84) * mm, "end": v(37.13, -9.83) * mm});
            skLineSegment(sketch, "E14.2.18.0", {"start": v(37.47, 4.94) * mm, "end": v(36.16, 4.77) * mm});
            skArc(sketch, "E14.3.18.0", {"start": v(34.4, 6.07) * mm, "mid": v(35.02, 5.06) * mm, "end": v(36.16, 4.77) * mm});
            skLineSegment(sketch, "E14.7.18.0", {"start": v(37.8, 0) * mm, "end": v(36.48, 0) * mm});
            skArc(sketch, "E14.10.18.0", {"start": v(36.48, 0) * mm, "mid": v(35.38, -0.45) * mm, "end": v(34.9, -1.53) * mm});
            skArc(sketch, "E14.14.18.0", {"start": v(38.1, 4.9) * mm, "mid": v(37.79, 4.95) * mm, "end": v(37.47, 4.94) * mm});
            skArc(sketch, "E14.18.18.0", {"start": v(38.1, 4.9) * mm, "mid": v(39.58, 4.35) * mm, "end": v(40.95, 3.57) * mm});
            skArc(sketch, "E14.22.18.0", {"start": v(41.16, 3.22) * mm, "mid": v(41.1, 3.41) * mm, "end": v(40.95, 3.57) * mm});
            skLineSegment(sketch, "E14.26.18.0", {"start": v(41.16, 3.22) * mm, "end": v(41.23, 2.7) * mm});
            skLineSegment(sketch, "E14.29.18.0", {"start": v(41.23, 2.18) * mm, "end": v(41.23, 2.7) * mm});
            skArc(sketch, "E14.32.18.0", {"start": v(41.06, 1.8) * mm, "mid": v(41.18, 1.98) * mm, "end": v(41.23, 2.18) * mm});
            skArc(sketch, "E14.36.18.0", {"start": v(38.41, 0.12) * mm, "mid": v(39.8, 0.85) * mm, "end": v(41.06, 1.8) * mm});
            skArc(sketch, "E14.40.18.0", {"start": v(37.8, 0) * mm, "mid": v(38.1, 0.02) * mm, "end": v(38.41, 0.12) * mm});
            skLineSegment(sketch, "E14.2.19.0", {"start": v(34.91, 14.47) * mm, "end": v(33.7, 13.97) * mm});
            skArc(sketch, "E14.3.19.0", {"start": v(31.65, 14.76) * mm, "mid": v(32.51, 13.95) * mm, "end": v(33.7, 13.97) * mm});
            skLineSegment(sketch, "E14.7.19.0", {"start": v(36.5, 9.77) * mm, "end": v(35.24, 9.43) * mm});
            skArc(sketch, "E14.10.19.0", {"start": v(35.24, 9.43) * mm, "mid": v(34.3, 8.72) * mm, "end": v(34.1, 7.56) * mm});
            skArc(sketch, "E14.14.19.0", {"start": v(35.53, 14.6) * mm, "mid": v(35.22, 14.56) * mm, "end": v(34.91, 14.47) * mm});
            skArc(sketch, "E14.18.19.0", {"start": v(35.53, 14.6) * mm, "mid": v(37.1, 14.45) * mm, "end": v(38.63, 14.04) * mm});
            skArc(sketch, "E14.22.19.0", {"start": v(38.93, 13.76) * mm, "mid": v(38.8, 13.93) * mm, "end": v(38.63, 14.04) * mm});
            skLineSegment(sketch, "E14.26.19.0", {"start": v(38.93, 13.76) * mm, "end": v(39.12, 13.28) * mm});
            skLineSegment(sketch, "E14.29.19.0", {"start": v(39.26, 12.78) * mm, "end": v(39.12, 13.28) * mm});
            skArc(sketch, "E14.32.19.0", {"start": v(39.2, 12.37) * mm, "mid": v(39.27, 12.57) * mm, "end": v(39.26, 12.78) * mm});
            skArc(sketch, "E14.36.19.0", {"start": v(37.07, 10.06) * mm, "mid": v(38.23, 11.13) * mm, "end": v(39.2, 12.37) * mm});
            skArc(sketch, "E14.40.19.0", {"start": v(36.5, 9.77) * mm, "mid": v(36.8, 9.89) * mm, "end": v(37.07, 10.06) * mm});
            skLineSegment(sketch, "E14.2.20.0", {"start": v(29.98, 23.01) * mm, "end": v(28.93, 22.21) * mm});
            skArc(sketch, "E14.3.20.0", {"start": v(26.75, 22.45) * mm, "mid": v(27.8, 21.9) * mm, "end": v(28.93, 22.21) * mm});
            skLineSegment(sketch, "E14.7.20.0", {"start": v(32.73, 18.89) * mm, "end": v(31.6, 18.23) * mm});
            skArc(sketch, "E14.10.20.0", {"start": v(31.6, 18.23) * mm, "mid": v(30.86, 17.3) * mm, "end": v(30.98, 16.12) * mm});
            skArc(sketch, "E14.14.20.0", {"start": v(30.55, 23.3) * mm, "mid": v(30.25, 23.18) * mm, "end": v(29.98, 23.01) * mm});
            skArc(sketch, "E14.18.20.0", {"start": v(30.55, 23.3) * mm, "mid": v(32.1, 23.56) * mm, "end": v(33.68, 23.56) * mm});
            skArc(sketch, "E14.22.20.0", {"start": v(34.04, 23.36) * mm, "mid": v(33.88, 23.5) * mm, "end": v(33.68, 23.56) * mm});
            skLineSegment(sketch, "E14.26.20.0", {"start": v(34.04, 23.36) * mm, "end": v(34.35, 22.95) * mm});
            skLineSegment(sketch, "E14.29.20.0", {"start": v(34.61, 22.5) * mm, "end": v(34.35, 22.95) * mm});
            skArc(sketch, "E14.32.20.0", {"start": v(34.66, 22.1) * mm, "mid": v(34.68, 22.3) * mm, "end": v(34.61, 22.5) * mm});
            skArc(sketch, "E14.36.20.0", {"start": v(33.2, 19.3) * mm, "mid": v(34.05, 20.64) * mm, "end": v(34.66, 22.1) * mm});
            skArc(sketch, "E14.40.20.0", {"start": v(32.73, 18.89) * mm, "mid": v(33, 19.07) * mm, "end": v(33.2, 19.3) * mm});
            skLineSegment(sketch, "E14.2.21.0", {"start": v(23, 29.99) * mm, "end": v(22.2, 28.94) * mm});
            skArc(sketch, "E14.3.21.0", {"start": v(20.03, 28.61) * mm, "mid": v(21.18, 28.34) * mm, "end": v(22.2, 28.94) * mm});
            skLineSegment(sketch, "E14.7.21.0", {"start": v(26.73, 26.72) * mm, "end": v(25.8, 25.79) * mm});
            skArc(sketch, "E14.10.21.0", {"start": v(25.8, 25.79) * mm, "mid": v(25.34, 24.7) * mm, "end": v(25.75, 23.6) * mm});
            skArc(sketch, "E14.14.21.0", {"start": v(23.48, 30.4) * mm, "mid": v(23.22, 30.22) * mm, "end": v(23, 29.99) * mm});
            skArc(sketch, "E14.18.21.0", {"start": v(23.48, 30.4) * mm, "mid": v(24.9, 31.06) * mm, "end": v(26.43, 31.48) * mm});
            skArc(sketch, "E14.22.21.0", {"start": v(26.83, 31.38) * mm, "mid": v(26.64, 31.47) * mm, "end": v(26.43, 31.48) * mm});
            skLineSegment(sketch, "E14.26.21.0", {"start": v(26.83, 31.38) * mm, "end": v(27.24, 31.06) * mm});
            skLineSegment(sketch, "E14.29.21.0", {"start": v(27.6, 30.7) * mm, "end": v(27.24, 31.06) * mm});
            skArc(sketch, "E14.32.21.0", {"start": v(27.76, 30.31) * mm, "mid": v(27.72, 30.52) * mm, "end": v(27.6, 30.7) * mm});
            skArc(sketch, "E14.36.21.0", {"start": v(27.08, 27.25) * mm, "mid": v(27.54, 28.75) * mm, "end": v(27.76, 30.31) * mm});
            skArc(sketch, "E14.40.21.0", {"start": v(26.73, 26.72) * mm, "mid": v(26.93, 26.96) * mm, "end": v(27.08, 27.25) * mm});
            skLineSegment(sketch, "E14.2.22.0", {"start": v(14.45, 34.92) * mm, "end": v(13.95, 33.7) * mm});
            skArc(sketch, "E14.3.22.0", {"start": v(11.94, 32.82) * mm, "mid": v(13.12, 32.86) * mm, "end": v(13.95, 33.7) * mm});
            skLineSegment(sketch, "E14.7.22.0", {"start": v(18.9, 32.72) * mm, "end": v(18.25, 31.59) * mm});
            skArc(sketch, "E14.10.22.0", {"start": v(18.25, 31.59) * mm, "mid": v(18.08, 30.42) * mm, "end": v(18.77, 29.45) * mm});
            skArc(sketch, "E14.14.22.0", {"start": v(14.8, 35.44) * mm, "mid": v(14.6, 35.2) * mm, "end": v(14.45, 34.92) * mm});
            skArc(sketch, "E14.18.22.0", {"start": v(14.8, 35.44) * mm, "mid": v(16.02, 36.45) * mm, "end": v(17.38, 37.24) * mm});
            skArc(sketch, "E14.22.22.0", {"start": v(17.8, 37.25) * mm, "mid": v(17.59, 37.3) * mm, "end": v(17.38, 37.24) * mm});
            skLineSegment(sketch, "E14.26.22.0", {"start": v(17.8, 37.25) * mm, "end": v(18.27, 37.06) * mm});
            skLineSegment(sketch, "E14.29.22.0", {"start": v(18.72, 36.8) * mm, "end": v(18.27, 37.06) * mm});
            skArc(sketch, "E14.32.22.0", {"start": v(18.96, 36.46) * mm, "mid": v(18.88, 36.66) * mm, "end": v(18.72, 36.8) * mm});
            skArc(sketch, "E14.36.22.0", {"start": v(19.1, 33.33) * mm, "mid": v(19.16, 34.9) * mm, "end": v(18.96, 36.46) * mm});
            skArc(sketch, "E14.40.22.0", {"start": v(18.9, 32.72) * mm, "mid": v(19.03, 33.01) * mm, "end": v(19.1, 33.33) * mm});
            skLineSegment(sketch, "E14.2.23.0", {"start": v(4.92, 37.47) * mm, "end": v(4.75, 36.17) * mm});
            skArc(sketch, "E14.3.23.0", {"start": v(3.04, 34.8) * mm, "mid": v(4.17, 35.14) * mm, "end": v(4.75, 36.17) * mm});
            skLineSegment(sketch, "E14.7.23.0", {"start": v(9.79, 36.5) * mm, "end": v(9.45, 35.23) * mm});
            skArc(sketch, "E14.10.23.0", {"start": v(9.45, 35.23) * mm, "mid": v(9.6, 34.06) * mm, "end": v(10.5, 33.3) * mm});
            skArc(sketch, "E14.14.23.0", {"start": v(5.13, 38.07) * mm, "mid": v(5, 37.78) * mm, "end": v(4.92, 37.47) * mm});
            skArc(sketch, "E14.18.23.0", {"start": v(5.13, 38.07) * mm, "mid": v(6.04, 39.36) * mm, "end": v(7.15, 40.47) * mm});
            skArc(sketch, "E14.22.23.0", {"start": v(7.55, 40.6) * mm, "mid": v(7.34, 40.57) * mm, "end": v(7.15, 40.47) * mm});
            skLineSegment(sketch, "E14.26.23.0", {"start": v(7.55, 40.6) * mm, "end": v(8.06, 40.52) * mm});
            skLineSegment(sketch, "E14.29.23.0", {"start": v(8.56, 40.39) * mm, "end": v(8.06, 40.52) * mm});
            skArc(sketch, "E14.32.23.0", {"start": v(8.88, 40.13) * mm, "mid": v(8.75, 40.3) * mm, "end": v(8.56, 40.39) * mm});
            skArc(sketch, "E14.36.23.0", {"start": v(9.83, 37.13) * mm, "mid": v(9.48, 38.67) * mm, "end": v(8.88, 40.13) * mm});
            skArc(sketch, "E14.40.23.0", {"start": v(9.79, 36.5) * mm, "mid": v(9.84, 36.82) * mm, "end": v(9.83, 37.13) * mm});
            skArc(sketch, "E15.trimOffspring", {"start": v(-28.61, 20.03) * mm, "mid": v(-29.04, 19.4) * mm, "end": v(-29.45, 18.77) * mm});
            skArc(sketch, "E16.trimOffspring", {"start": v(-22.45, 26.75) * mm, "mid": v(-23.03, 26.26) * mm, "end": v(-23.6, 25.75) * mm});
            skArc(sketch, "E17.trimOffspring", {"start": v(-14.76, 31.65) * mm, "mid": v(-15.45, 31.32) * mm, "end": v(-16.12, 30.98) * mm});
            skArc(sketch, "E18.trimOffspring", {"start": v(3.04, 34.8) * mm, "mid": v(2.28, 34.85) * mm, "end": v(1.53, 34.9) * mm});
            skArc(sketch, "E19.trimOffspring", {"start": v(11.94, 32.82) * mm, "mid": v(11.23, 33.07) * mm, "end": v(10.5, 33.3) * mm});
            skArc(sketch, "E20.trimOffspring", {"start": v(20.03, 28.61) * mm, "mid": v(19.4, 29.04) * mm, "end": v(18.77, 29.45) * mm});
            skArc(sketch, "E21.trimOffspring", {"start": v(26.75, 22.45) * mm, "mid": v(26.26, 23.03) * mm, "end": v(25.75, 23.6) * mm});
            skArc(sketch, "E22.trimOffspring", {"start": v(31.65, 14.76) * mm, "mid": v(31.32, 15.45) * mm, "end": v(30.98, 16.12) * mm});
            skArc(sketch, "E23.trimOffspring", {"start": v(34.4, 6.07) * mm, "mid": v(34.25, 6.81) * mm, "end": v(34.1, 7.56) * mm});
            skArc(sketch, "E24.trimOffspring", {"start": v(-34.8, 3.04) * mm, "mid": v(-34.85, 2.28) * mm, "end": v(-34.9, 1.53) * mm});
            skArc(sketch, "E25.trimOffspring", {"start": v(-32.82, 11.94) * mm, "mid": v(-33.07, 11.23) * mm, "end": v(-33.3, 10.5) * mm});
            skArc(sketch, "E26.trimOffspring", {"start": v(-34.4, -6.07) * mm, "mid": v(-34.25, -6.81) * mm, "end": v(-34.1, -7.56) * mm});
            skArc(sketch, "E27.trimOffspring", {"start": v(-31.65, -14.76) * mm, "mid": v(-31.32, -15.45) * mm, "end": v(-30.98, -16.12) * mm});
            skArc(sketch, "E28.trimOffspring", {"start": v(-26.75, -22.45) * mm, "mid": v(-26.26, -23.03) * mm, "end": v(-25.75, -23.6) * mm});
            skArc(sketch, "E29.trimOffspring", {"start": v(-11.94, -32.82) * mm, "mid": v(-11.23, -33.07) * mm, "end": v(-10.5, -33.3) * mm});
            skArc(sketch, "E30.trimOffspring", {"start": v(-20.03, -28.61) * mm, "mid": v(-19.4, -29.04) * mm, "end": v(-18.77, -29.45) * mm});
            skArc(sketch, "E31.trimOffspring", {"start": v(-3.04, -34.8) * mm, "mid": v(-2.28, -34.85) * mm, "end": v(-1.53, -34.9) * mm});
            skArc(sketch, "E32.trimOffspring", {"start": v(6.07, -34.4) * mm, "mid": v(6.81, -34.25) * mm, "end": v(7.56, -34.1) * mm});
            skArc(sketch, "E33.trimOffspring", {"start": v(14.76, -31.65) * mm, "mid": v(15.45, -31.32) * mm, "end": v(16.12, -30.98) * mm});
            skArc(sketch, "E34.trimOffspring", {"start": v(22.45, -26.75) * mm, "mid": v(23.03, -26.26) * mm, "end": v(23.6, -25.75) * mm});
            skArc(sketch, "E35.trimOffspring", {"start": v(34.8, -3.04) * mm, "mid": v(34.85, -2.28) * mm, "end": v(34.9, -1.53) * mm});
            skArc(sketch, "E36.trimOffspring", {"start": v(32.82, -11.94) * mm, "mid": v(33.07, -11.23) * mm, "end": v(33.3, -10.5) * mm});
            skArc(sketch, "E37.trimOffspring", {"start": v(28.61, -20.03) * mm, "mid": v(29.04, -19.4) * mm, "end": v(29.45, -18.77) * mm});
            skSolve(sketch);
        }
        {
            var Q0;
            Q0=makeQuery(id+"F0.imprint","IMPRINT",FACE,{"disambiguationData":[TD([[makeQuery(id+"F0.imprint","IMPRINT",EDGE,{"derivedFrom":sQuery(id+"F0.wireOp",EDGE,"E0")}),1.0]])]});
            cPlane(context, id + "F1", {"entities" : qUnion([Q0]), "cplaneType" : CPlaneType.OFFSET, "offset" : 50.8 * mm, "width" : 152.4 * mm, "height" : 152.4 * mm});
        }
        {
            var Q0;
            Q0=qCreatedBy(id+"F1.planeOp",FACE);
            var sketch = newSketch(context, id + "F2", { "sketchPlane" : qUnion([Q0])});
            skArc(sketch, "E38.0.0", {"start": v(-38.1, -4.9) * mm, "mid": v(-37.79, -4.95) * mm, "end": v(-37.47, -4.94) * mm});
            skLineSegment(sketch, "E38.0.1", {"start": v(-37.47, -4.94) * mm, "end": v(-36.16, -4.77) * mm});
            skArc(sketch, "E38.0.2", {"start": v(-36.16, -4.77) * mm, "mid": v(-35.02, -5.06) * mm, "end": v(-34.4, -6.07) * mm});
            skArc(sketch, "E38.0.3", {"start": v(-34.4, -6.07) * mm, "mid": v(-34.25, -6.81) * mm, "end": v(-34.1, -7.56) * mm});
            skArc(sketch, "E38.0.4", {"start": v(-34.1, -7.56) * mm, "mid": v(-34.3, -8.72) * mm, "end": v(-35.24, -9.43) * mm});
            skLineSegment(sketch, "E38.0.5", {"start": v(-35.24, -9.43) * mm, "end": v(-36.5, -9.77) * mm});
            skArc(sketch, "E38.0.6", {"start": v(-36.5, -9.77) * mm, "mid": v(-36.8, -9.89) * mm, "end": v(-37.07, -10.06) * mm});
            skArc(sketch, "E38.0.7", {"start": v(-37.07, -10.06) * mm, "mid": v(-38.23, -11.13) * mm, "end": v(-39.2, -12.37) * mm});
            skArc(sketch, "E38.0.8", {"start": v(-39.2, -12.37) * mm, "mid": v(-39.27, -12.57) * mm, "end": v(-39.26, -12.78) * mm});
            skLineSegment(sketch, "E38.0.9", {"start": v(-39.26, -12.78) * mm, "end": v(-39.12, -13.28) * mm});
            skLineSegment(sketch, "E38.0.10", {"start": v(-39.12, -13.28) * mm, "end": v(-38.93, -13.76) * mm});
            skArc(sketch, "E38.0.11", {"start": v(-38.93, -13.76) * mm, "mid": v(-38.8, -13.93) * mm, "end": v(-38.63, -14.04) * mm});
            skArc(sketch, "E38.0.12", {"start": v(-38.63, -14.04) * mm, "mid": v(-37.1, -14.45) * mm, "end": v(-35.53, -14.6) * mm});
            skArc(sketch, "E38.0.13", {"start": v(-35.53, -14.6) * mm, "mid": v(-35.22, -14.56) * mm, "end": v(-34.91, -14.47) * mm});
            skLineSegment(sketch, "E38.0.14", {"start": v(-34.91, -14.47) * mm, "end": v(-33.7, -13.97) * mm});
            skArc(sketch, "E38.0.15", {"start": v(-33.7, -13.97) * mm, "mid": v(-32.51, -13.95) * mm, "end": v(-31.65, -14.76) * mm});
            skArc(sketch, "E38.0.16", {"start": v(-31.65, -14.76) * mm, "mid": v(-31.32, -15.45) * mm, "end": v(-30.98, -16.12) * mm});
            skArc(sketch, "E38.0.17", {"start": v(-30.98, -16.12) * mm, "mid": v(-30.86, -17.3) * mm, "end": v(-31.6, -18.23) * mm});
            skLineSegment(sketch, "E38.0.18", {"start": v(-31.6, -18.23) * mm, "end": v(-32.73, -18.89) * mm});
            skArc(sketch, "E38.0.19", {"start": v(-32.73, -18.89) * mm, "mid": v(-33, -19.07) * mm, "end": v(-33.2, -19.3) * mm});
            skArc(sketch, "E38.0.20", {"start": v(-33.2, -19.3) * mm, "mid": v(-34.05, -20.64) * mm, "end": v(-34.66, -22.1) * mm});
            skArc(sketch, "E38.0.21", {"start": v(-34.66, -22.1) * mm, "mid": v(-34.68, -22.3) * mm, "end": v(-34.61, -22.5) * mm});
            skLineSegment(sketch, "E38.0.22", {"start": v(-34.61, -22.5) * mm, "end": v(-34.35, -22.95) * mm});
            skLineSegment(sketch, "E38.0.23", {"start": v(-34.35, -22.95) * mm, "end": v(-34.04, -23.36) * mm});
            skArc(sketch, "E38.0.24", {"start": v(-34.04, -23.36) * mm, "mid": v(-33.88, -23.5) * mm, "end": v(-33.68, -23.56) * mm});
            skArc(sketch, "E38.0.25", {"start": v(-33.68, -23.56) * mm, "mid": v(-32.1, -23.56) * mm, "end": v(-30.55, -23.3) * mm});
            skArc(sketch, "E38.0.26", {"start": v(-30.55, -23.3) * mm, "mid": v(-30.25, -23.18) * mm, "end": v(-29.98, -23.01) * mm});
            skLineSegment(sketch, "E38.0.27", {"start": v(-29.98, -23.01) * mm, "end": v(-28.93, -22.21) * mm});
            skArc(sketch, "E38.0.28", {"start": v(-28.93, -22.21) * mm, "mid": v(-27.8, -21.9) * mm, "end": v(-26.75, -22.45) * mm});
            skArc(sketch, "E38.0.29", {"start": v(-26.75, -22.45) * mm, "mid": v(-26.26, -23.03) * mm, "end": v(-25.75, -23.6) * mm});
            skArc(sketch, "E38.0.30", {"start": v(-25.75, -23.6) * mm, "mid": v(-25.34, -24.7) * mm, "end": v(-25.8, -25.79) * mm});
            skLineSegment(sketch, "E38.0.31", {"start": v(-25.8, -25.79) * mm, "end": v(-26.73, -26.72) * mm});
            skArc(sketch, "E38.0.32", {"start": v(-26.73, -26.72) * mm, "mid": v(-26.93, -26.96) * mm, "end": v(-27.08, -27.25) * mm});
            skArc(sketch, "E38.0.33", {"start": v(-27.08, -27.25) * mm, "mid": v(-27.54, -28.75) * mm, "end": v(-27.76, -30.31) * mm});
            skArc(sketch, "E38.0.34", {"start": v(-27.76, -30.31) * mm, "mid": v(-27.72, -30.52) * mm, "end": v(-27.6, -30.7) * mm});
            skLineSegment(sketch, "E38.0.35", {"start": v(-27.6, -30.7) * mm, "end": v(-27.24, -31.06) * mm});
            skLineSegment(sketch, "E38.0.36", {"start": v(-27.24, -31.06) * mm, "end": v(-26.83, -31.38) * mm});
            skArc(sketch, "E38.0.37", {"start": v(-26.83, -31.38) * mm, "mid": v(-26.64, -31.47) * mm, "end": v(-26.43, -31.48) * mm});
            skArc(sketch, "E38.0.38", {"start": v(-26.43, -31.48) * mm, "mid": v(-24.9, -31.06) * mm, "end": v(-23.48, -30.4) * mm});
            skArc(sketch, "E38.0.39", {"start": v(-23.48, -30.4) * mm, "mid": v(-23.22, -30.22) * mm, "end": v(-23, -29.99) * mm});
            skLineSegment(sketch, "E38.0.40", {"start": v(-23, -29.99) * mm, "end": v(-22.2, -28.94) * mm});
            skArc(sketch, "E38.0.41", {"start": v(-22.2, -28.94) * mm, "mid": v(-21.18, -28.34) * mm, "end": v(-20.03, -28.61) * mm});
            skArc(sketch, "E38.0.42", {"start": v(-20.03, -28.61) * mm, "mid": v(-19.4, -29.04) * mm, "end": v(-18.77, -29.45) * mm});
            skArc(sketch, "E38.0.43", {"start": v(-18.77, -29.45) * mm, "mid": v(-18.08, -30.42) * mm, "end": v(-18.25, -31.59) * mm});
            skLineSegment(sketch, "E38.0.44", {"start": v(-18.25, -31.59) * mm, "end": v(-18.9, -32.72) * mm});
            skArc(sketch, "E38.0.45", {"start": v(-18.9, -32.72) * mm, "mid": v(-19.03, -33.01) * mm, "end": v(-19.1, -33.33) * mm});
            skArc(sketch, "E38.0.46", {"start": v(-19.1, -33.33) * mm, "mid": v(-19.16, -34.9) * mm, "end": v(-18.96, -36.46) * mm});
            skArc(sketch, "E38.0.47", {"start": v(-18.96, -36.46) * mm, "mid": v(-18.88, -36.66) * mm, "end": v(-18.72, -36.8) * mm});
            skLineSegment(sketch, "E38.0.48", {"start": v(-18.72, -36.8) * mm, "end": v(-18.27, -37.06) * mm});
            skLineSegment(sketch, "E38.0.49", {"start": v(-18.27, -37.06) * mm, "end": v(-17.8, -37.25) * mm});
            skArc(sketch, "E38.0.50", {"start": v(-17.8, -37.25) * mm, "mid": v(-17.59, -37.3) * mm, "end": v(-17.38, -37.24) * mm});
            skArc(sketch, "E38.0.51", {"start": v(-17.38, -37.24) * mm, "mid": v(-16.02, -36.45) * mm, "end": v(-14.8, -35.44) * mm});
            skArc(sketch, "E38.0.52", {"start": v(-14.8, -35.44) * mm, "mid": v(-14.6, -35.2) * mm, "end": v(-14.45, -34.92) * mm});
            skLineSegment(sketch, "E38.0.53", {"start": v(-14.45, -34.92) * mm, "end": v(-13.95, -33.7) * mm});
            skArc(sketch, "E38.0.54", {"start": v(-13.95, -33.7) * mm, "mid": v(-13.12, -32.86) * mm, "end": v(-11.94, -32.82) * mm});
            skArc(sketch, "E38.0.55", {"start": v(-11.94, -32.82) * mm, "mid": v(-11.23, -33.07) * mm, "end": v(-10.5, -33.3) * mm});
            skArc(sketch, "E38.0.56", {"start": v(-10.5, -33.3) * mm, "mid": v(-9.6, -34.06) * mm, "end": v(-9.45, -35.23) * mm});
            skLineSegment(sketch, "E38.0.57", {"start": v(-9.45, -35.23) * mm, "end": v(-9.79, -36.5) * mm});
            skArc(sketch, "E38.0.58", {"start": v(-9.79, -36.5) * mm, "mid": v(-9.84, -36.82) * mm, "end": v(-9.83, -37.13) * mm});
            skArc(sketch, "E38.0.59", {"start": v(-9.83, -37.13) * mm, "mid": v(-9.48, -38.67) * mm, "end": v(-8.88, -40.13) * mm});
            skArc(sketch, "E38.0.60", {"start": v(-8.88, -40.13) * mm, "mid": v(-8.75, -40.3) * mm, "end": v(-8.56, -40.39) * mm});
            skLineSegment(sketch, "E38.0.61", {"start": v(-8.56, -40.39) * mm, "end": v(-8.06, -40.52) * mm});
            skLineSegment(sketch, "E38.0.62", {"start": v(-8.06, -40.52) * mm, "end": v(-7.55, -40.6) * mm});
            skArc(sketch, "E38.0.63", {"start": v(-7.55, -40.6) * mm, "mid": v(-7.34, -40.57) * mm, "end": v(-7.15, -40.47) * mm});
            skArc(sketch, "E38.0.64", {"start": v(-7.15, -40.47) * mm, "mid": v(-6.04, -39.36) * mm, "end": v(-5.13, -38.07) * mm});
            skArc(sketch, "E38.0.65", {"start": v(-5.13, -38.07) * mm, "mid": v(-5, -37.78) * mm, "end": v(-4.92, -37.47) * mm});
            skLineSegment(sketch, "E38.0.66", {"start": v(-4.92, -37.47) * mm, "end": v(-4.75, -36.17) * mm});
            skArc(sketch, "E38.0.67", {"start": v(-4.75, -36.17) * mm, "mid": v(-4.17, -35.14) * mm, "end": v(-3.04, -34.8) * mm});
            skArc(sketch, "E38.0.68", {"start": v(-3.04, -34.8) * mm, "mid": v(-2.28, -34.85) * mm, "end": v(-1.53, -34.9) * mm});
            skArc(sketch, "E38.0.69", {"start": v(-1.53, -34.9) * mm, "mid": v(-0.45, -35.38) * mm, "end": v(0, -36.48) * mm});
            skLineSegment(sketch, "E38.0.70", {"start": v(0, -36.48) * mm, "end": v(0, -37.8) * mm});
            skArc(sketch, "E38.0.71", {"start": v(0, -37.8) * mm, "mid": v(0.02, -38.1) * mm, "end": v(0.12, -38.41) * mm});
            skArc(sketch, "E38.0.72", {"start": v(0.12, -38.41) * mm, "mid": v(0.85, -39.8) * mm, "end": v(1.8, -41.06) * mm});
            skArc(sketch, "E38.0.73", {"start": v(1.8, -41.06) * mm, "mid": v(1.98, -41.18) * mm, "end": v(2.18, -41.23) * mm});
            skLineSegment(sketch, "E38.0.74", {"start": v(2.18, -41.23) * mm, "end": v(2.7, -41.23) * mm});
            skLineSegment(sketch, "E38.0.75", {"start": v(2.7, -41.23) * mm, "end": v(3.22, -41.16) * mm});
            skArc(sketch, "E38.0.76", {"start": v(3.22, -41.16) * mm, "mid": v(3.41, -41.1) * mm, "end": v(3.57, -40.95) * mm});
            skArc(sketch, "E38.0.77", {"start": v(3.57, -40.95) * mm, "mid": v(4.35, -39.58) * mm, "end": v(4.9, -38.1) * mm});
            skArc(sketch, "E38.0.78", {"start": v(4.9, -38.1) * mm, "mid": v(4.95, -37.79) * mm, "end": v(4.94, -37.47) * mm});
            skLineSegment(sketch, "E38.0.79", {"start": v(4.94, -37.47) * mm, "end": v(4.77, -36.16) * mm});
            skArc(sketch, "E38.0.80", {"start": v(4.77, -36.16) * mm, "mid": v(5.06, -35.02) * mm, "end": v(6.07, -34.4) * mm});
            skArc(sketch, "E38.0.81", {"start": v(6.07, -34.4) * mm, "mid": v(6.81, -34.25) * mm, "end": v(7.56, -34.1) * mm});
            skArc(sketch, "E38.0.82", {"start": v(7.56, -34.1) * mm, "mid": v(8.72, -34.3) * mm, "end": v(9.43, -35.24) * mm});
            skLineSegment(sketch, "E38.0.83", {"start": v(9.43, -35.24) * mm, "end": v(9.77, -36.5) * mm});
            skArc(sketch, "E38.0.84", {"start": v(9.77, -36.5) * mm, "mid": v(9.89, -36.8) * mm, "end": v(10.06, -37.07) * mm});
            skArc(sketch, "E38.0.85", {"start": v(10.06, -37.07) * mm, "mid": v(11.13, -38.23) * mm, "end": v(12.37, -39.2) * mm});
            skArc(sketch, "E38.0.86", {"start": v(12.37, -39.2) * mm, "mid": v(12.57, -39.27) * mm, "end": v(12.78, -39.26) * mm});
            skLineSegment(sketch, "E38.0.87", {"start": v(12.78, -39.26) * mm, "end": v(13.28, -39.12) * mm});
            skLineSegment(sketch, "E38.0.88", {"start": v(13.28, -39.12) * mm, "end": v(13.76, -38.93) * mm});
            skArc(sketch, "E38.0.89", {"start": v(13.76, -38.93) * mm, "mid": v(13.93, -38.8) * mm, "end": v(14.04, -38.63) * mm});
            skArc(sketch, "E38.0.90", {"start": v(14.04, -38.63) * mm, "mid": v(14.45, -37.1) * mm, "end": v(14.6, -35.53) * mm});
            skArc(sketch, "E38.0.91", {"start": v(14.6, -35.53) * mm, "mid": v(14.56, -35.22) * mm, "end": v(14.47, -34.91) * mm});
            skLineSegment(sketch, "E38.0.92", {"start": v(14.47, -34.91) * mm, "end": v(13.97, -33.7) * mm});
            skArc(sketch, "E38.0.93", {"start": v(13.97, -33.7) * mm, "mid": v(13.95, -32.51) * mm, "end": v(14.76, -31.65) * mm});
            skArc(sketch, "E38.0.94", {"start": v(14.76, -31.65) * mm, "mid": v(15.45, -31.32) * mm, "end": v(16.12, -30.98) * mm});
            skArc(sketch, "E38.0.95", {"start": v(16.12, -30.98) * mm, "mid": v(17.3, -30.86) * mm, "end": v(18.23, -31.6) * mm});
            skLineSegment(sketch, "E38.0.96", {"start": v(18.23, -31.6) * mm, "end": v(18.89, -32.73) * mm});
            skArc(sketch, "E38.0.97", {"start": v(18.89, -32.73) * mm, "mid": v(19.07, -33) * mm, "end": v(19.3, -33.2) * mm});
            skArc(sketch, "E38.0.98", {"start": v(19.3, -33.2) * mm, "mid": v(20.64, -34.05) * mm, "end": v(22.1, -34.66) * mm});
            skArc(sketch, "E38.0.99", {"start": v(22.1, -34.66) * mm, "mid": v(22.3, -34.68) * mm, "end": v(22.5, -34.61) * mm});
            skLineSegment(sketch, "E38.0.100", {"start": v(22.5, -34.61) * mm, "end": v(22.95, -34.35) * mm});
            skLineSegment(sketch, "E38.0.101", {"start": v(22.95, -34.35) * mm, "end": v(23.36, -34.04) * mm});
            skArc(sketch, "E38.0.102", {"start": v(23.36, -34.04) * mm, "mid": v(23.5, -33.88) * mm, "end": v(23.56, -33.68) * mm});
            skArc(sketch, "E38.0.103", {"start": v(23.56, -33.68) * mm, "mid": v(23.56, -32.1) * mm, "end": v(23.3, -30.55) * mm});
            skArc(sketch, "E38.0.104", {"start": v(23.3, -30.55) * mm, "mid": v(23.18, -30.25) * mm, "end": v(23.01, -29.98) * mm});
            skLineSegment(sketch, "E38.0.105", {"start": v(23.01, -29.98) * mm, "end": v(22.21, -28.93) * mm});
            skArc(sketch, "E38.0.106", {"start": v(22.21, -28.93) * mm, "mid": v(21.9, -27.8) * mm, "end": v(22.45, -26.75) * mm});
            skArc(sketch, "E38.0.107", {"start": v(22.45, -26.75) * mm, "mid": v(23.03, -26.26) * mm, "end": v(23.6, -25.75) * mm});
            skArc(sketch, "E38.0.108", {"start": v(23.6, -25.75) * mm, "mid": v(24.7, -25.34) * mm, "end": v(25.79, -25.8) * mm});
            skLineSegment(sketch, "E38.0.109", {"start": v(25.79, -25.8) * mm, "end": v(26.72, -26.73) * mm});
            skArc(sketch, "E38.0.110", {"start": v(26.72, -26.73) * mm, "mid": v(26.96, -26.93) * mm, "end": v(27.25, -27.08) * mm});
            skArc(sketch, "E38.0.111", {"start": v(27.25, -27.08) * mm, "mid": v(28.75, -27.54) * mm, "end": v(30.31, -27.76) * mm});
            skArc(sketch, "E38.0.112", {"start": v(30.31, -27.76) * mm, "mid": v(30.52, -27.72) * mm, "end": v(30.7, -27.6) * mm});
            skLineSegment(sketch, "E38.0.113", {"start": v(30.7, -27.6) * mm, "end": v(31.06, -27.24) * mm});
            skLineSegment(sketch, "E38.0.114", {"start": v(31.06, -27.24) * mm, "end": v(31.38, -26.83) * mm});
            skArc(sketch, "E38.0.115", {"start": v(31.38, -26.83) * mm, "mid": v(31.47, -26.64) * mm, "end": v(31.48, -26.43) * mm});
            skArc(sketch, "E38.0.116", {"start": v(31.48, -26.43) * mm, "mid": v(31.06, -24.9) * mm, "end": v(30.4, -23.48) * mm});
            skArc(sketch, "E38.0.117", {"start": v(30.4, -23.48) * mm, "mid": v(30.22, -23.22) * mm, "end": v(29.99, -23) * mm});
            skLineSegment(sketch, "E38.0.118", {"start": v(29.99, -23) * mm, "end": v(28.94, -22.2) * mm});
            skArc(sketch, "E38.0.119", {"start": v(28.94, -22.2) * mm, "mid": v(28.34, -21.18) * mm, "end": v(28.61, -20.03) * mm});
            skArc(sketch, "E38.0.120", {"start": v(28.61, -20.03) * mm, "mid": v(29.04, -19.4) * mm, "end": v(29.45, -18.77) * mm});
            skArc(sketch, "E38.0.121", {"start": v(29.45, -18.77) * mm, "mid": v(30.42, -18.08) * mm, "end": v(31.59, -18.25) * mm});
            skLineSegment(sketch, "E38.0.122", {"start": v(31.59, -18.25) * mm, "end": v(32.72, -18.9) * mm});
            skArc(sketch, "E38.0.123", {"start": v(32.72, -18.9) * mm, "mid": v(33.01, -19.03) * mm, "end": v(33.33, -19.1) * mm});
            skArc(sketch, "E38.0.124", {"start": v(33.33, -19.1) * mm, "mid": v(34.9, -19.16) * mm, "end": v(36.46, -18.96) * mm});
            skArc(sketch, "E38.0.125", {"start": v(36.46, -18.96) * mm, "mid": v(36.66, -18.88) * mm, "end": v(36.8, -18.72) * mm});
            skLineSegment(sketch, "E38.0.126", {"start": v(36.8, -18.72) * mm, "end": v(37.06, -18.27) * mm});
            skLineSegment(sketch, "E38.0.127", {"start": v(37.06, -18.27) * mm, "end": v(37.25, -17.8) * mm});
            skArc(sketch, "E38.0.128", {"start": v(37.25, -17.8) * mm, "mid": v(37.3, -17.59) * mm, "end": v(37.24, -17.38) * mm});
            skArc(sketch, "E38.0.129", {"start": v(37.24, -17.38) * mm, "mid": v(36.45, -16.02) * mm, "end": v(35.44, -14.8) * mm});
            skArc(sketch, "E38.0.130", {"start": v(35.44, -14.8) * mm, "mid": v(35.2, -14.6) * mm, "end": v(34.92, -14.45) * mm});
            skLineSegment(sketch, "E38.0.131", {"start": v(34.92, -14.45) * mm, "end": v(33.7, -13.95) * mm});
            skArc(sketch, "E38.0.132", {"start": v(33.7, -13.95) * mm, "mid": v(32.86, -13.12) * mm, "end": v(32.82, -11.94) * mm});
            skArc(sketch, "E38.0.133", {"start": v(32.82, -11.94) * mm, "mid": v(33.07, -11.23) * mm, "end": v(33.3, -10.5) * mm});
            skArc(sketch, "E38.0.134", {"start": v(33.3, -10.5) * mm, "mid": v(34.06, -9.6) * mm, "end": v(35.23, -9.45) * mm});
            skLineSegment(sketch, "E38.0.135", {"start": v(35.23, -9.45) * mm, "end": v(36.5, -9.79) * mm});
            skArc(sketch, "E38.0.136", {"start": v(36.5, -9.79) * mm, "mid": v(36.82, -9.84) * mm, "end": v(37.13, -9.83) * mm});
            skArc(sketch, "E38.0.137", {"start": v(37.13, -9.83) * mm, "mid": v(38.67, -9.48) * mm, "end": v(40.13, -8.88) * mm});
            skArc(sketch, "E38.0.138", {"start": v(40.13, -8.88) * mm, "mid": v(40.3, -8.75) * mm, "end": v(40.39, -8.56) * mm});
            skLineSegment(sketch, "E38.0.139", {"start": v(40.39, -8.56) * mm, "end": v(40.52, -8.06) * mm});
            skLineSegment(sketch, "E38.0.140", {"start": v(40.52, -8.06) * mm, "end": v(40.6, -7.55) * mm});
            skArc(sketch, "E38.0.141", {"start": v(40.6, -7.55) * mm, "mid": v(40.57, -7.34) * mm, "end": v(40.47, -7.15) * mm});
            skArc(sketch, "E38.0.142", {"start": v(40.47, -7.15) * mm, "mid": v(39.36, -6.04) * mm, "end": v(38.07, -5.13) * mm});
            skArc(sketch, "E38.0.143", {"start": v(38.07, -5.13) * mm, "mid": v(37.78, -5) * mm, "end": v(37.47, -4.92) * mm});
            skLineSegment(sketch, "E38.0.144", {"start": v(37.47, -4.92) * mm, "end": v(36.17, -4.75) * mm});
            skArc(sketch, "E38.0.145", {"start": v(36.17, -4.75) * mm, "mid": v(35.14, -4.17) * mm, "end": v(34.8, -3.04) * mm});
            skArc(sketch, "E38.0.146", {"start": v(34.8, -3.04) * mm, "mid": v(34.85, -2.28) * mm, "end": v(34.9, -1.53) * mm});
            skArc(sketch, "E38.0.147", {"start": v(34.9, -1.53) * mm, "mid": v(35.38, -0.45) * mm, "end": v(36.48, 0) * mm});
            skLineSegment(sketch, "E38.0.148", {"start": v(36.48, 0) * mm, "end": v(37.8, 0) * mm});
            skArc(sketch, "E38.0.149", {"start": v(37.8, 0) * mm, "mid": v(38.1, 0.02) * mm, "end": v(38.41, 0.12) * mm});
            skArc(sketch, "E38.0.150", {"start": v(38.41, 0.12) * mm, "mid": v(39.8, 0.85) * mm, "end": v(41.06, 1.8) * mm});
            skArc(sketch, "E38.0.151", {"start": v(41.06, 1.8) * mm, "mid": v(41.18, 1.98) * mm, "end": v(41.23, 2.18) * mm});
            skLineSegment(sketch, "E38.0.152", {"start": v(41.23, 2.18) * mm, "end": v(41.23, 2.7) * mm});
            skLineSegment(sketch, "E38.0.153", {"start": v(41.23, 2.7) * mm, "end": v(41.16, 3.22) * mm});
            skArc(sketch, "E38.0.154", {"start": v(41.16, 3.22) * mm, "mid": v(41.1, 3.41) * mm, "end": v(40.95, 3.57) * mm});
            skArc(sketch, "E38.0.155", {"start": v(40.95, 3.57) * mm, "mid": v(39.58, 4.35) * mm, "end": v(38.1, 4.9) * mm});
            skArc(sketch, "E38.0.156", {"start": v(38.1, 4.9) * mm, "mid": v(37.79, 4.95) * mm, "end": v(37.47, 4.94) * mm});
            skLineSegment(sketch, "E38.0.157", {"start": v(37.47, 4.94) * mm, "end": v(36.16, 4.77) * mm});
            skArc(sketch, "E38.0.158", {"start": v(36.16, 4.77) * mm, "mid": v(35.02, 5.06) * mm, "end": v(34.4, 6.07) * mm});
            skArc(sketch, "E38.0.159", {"start": v(34.4, 6.07) * mm, "mid": v(34.25, 6.81) * mm, "end": v(34.1, 7.56) * mm});
            skArc(sketch, "E38.0.160", {"start": v(34.1, 7.56) * mm, "mid": v(34.3, 8.72) * mm, "end": v(35.24, 9.43) * mm});
            skLineSegment(sketch, "E38.0.161", {"start": v(35.24, 9.43) * mm, "end": v(36.5, 9.77) * mm});
            skArc(sketch, "E38.0.162", {"start": v(36.5, 9.77) * mm, "mid": v(36.8, 9.89) * mm, "end": v(37.07, 10.06) * mm});
            skArc(sketch, "E38.0.163", {"start": v(37.07, 10.06) * mm, "mid": v(38.23, 11.13) * mm, "end": v(39.2, 12.37) * mm});
            skArc(sketch, "E38.0.164", {"start": v(39.2, 12.37) * mm, "mid": v(39.27, 12.57) * mm, "end": v(39.26, 12.78) * mm});
            skLineSegment(sketch, "E38.0.165", {"start": v(39.26, 12.78) * mm, "end": v(39.12, 13.28) * mm});
            skLineSegment(sketch, "E38.0.166", {"start": v(39.12, 13.28) * mm, "end": v(38.93, 13.76) * mm});
            skArc(sketch, "E38.0.167", {"start": v(38.93, 13.76) * mm, "mid": v(38.8, 13.93) * mm, "end": v(38.63, 14.04) * mm});
            skArc(sketch, "E38.0.168", {"start": v(38.63, 14.04) * mm, "mid": v(37.1, 14.45) * mm, "end": v(35.53, 14.6) * mm});
            skArc(sketch, "E38.0.169", {"start": v(35.53, 14.6) * mm, "mid": v(35.22, 14.56) * mm, "end": v(34.91, 14.47) * mm});
            skLineSegment(sketch, "E38.0.170", {"start": v(34.91, 14.47) * mm, "end": v(33.7, 13.97) * mm});
            skArc(sketch, "E38.0.171", {"start": v(33.7, 13.97) * mm, "mid": v(32.51, 13.95) * mm, "end": v(31.65, 14.76) * mm});
            skArc(sketch, "E38.0.172", {"start": v(31.65, 14.76) * mm, "mid": v(31.32, 15.45) * mm, "end": v(30.98, 16.12) * mm});
            skArc(sketch, "E38.0.173", {"start": v(30.98, 16.12) * mm, "mid": v(30.86, 17.3) * mm, "end": v(31.6, 18.23) * mm});
            skLineSegment(sketch, "E38.0.174", {"start": v(31.6, 18.23) * mm, "end": v(32.73, 18.89) * mm});
            skArc(sketch, "E38.0.175", {"start": v(32.73, 18.89) * mm, "mid": v(33, 19.07) * mm, "end": v(33.2, 19.3) * mm});
            skArc(sketch, "E38.0.176", {"start": v(33.2, 19.3) * mm, "mid": v(34.05, 20.64) * mm, "end": v(34.66, 22.1) * mm});
            skArc(sketch, "E38.0.177", {"start": v(34.66, 22.1) * mm, "mid": v(34.68, 22.3) * mm, "end": v(34.61, 22.5) * mm});
            skLineSegment(sketch, "E38.0.178", {"start": v(34.61, 22.5) * mm, "end": v(34.35, 22.95) * mm});
            skLineSegment(sketch, "E38.0.179", {"start": v(34.35, 22.95) * mm, "end": v(34.04, 23.36) * mm});
            skArc(sketch, "E38.0.180", {"start": v(34.04, 23.36) * mm, "mid": v(33.88, 23.5) * mm, "end": v(33.68, 23.56) * mm});
            skArc(sketch, "E38.0.181", {"start": v(33.68, 23.56) * mm, "mid": v(32.1, 23.56) * mm, "end": v(30.55, 23.3) * mm});
            skArc(sketch, "E38.0.182", {"start": v(30.55, 23.3) * mm, "mid": v(30.25, 23.18) * mm, "end": v(29.98, 23.01) * mm});
            skLineSegment(sketch, "E38.0.183", {"start": v(29.98, 23.01) * mm, "end": v(28.93, 22.21) * mm});
            skArc(sketch, "E38.0.184", {"start": v(28.93, 22.21) * mm, "mid": v(27.8, 21.9) * mm, "end": v(26.75, 22.45) * mm});
            skArc(sketch, "E38.0.185", {"start": v(26.75, 22.45) * mm, "mid": v(26.26, 23.03) * mm, "end": v(25.75, 23.6) * mm});
            skArc(sketch, "E38.0.186", {"start": v(25.75, 23.6) * mm, "mid": v(25.34, 24.7) * mm, "end": v(25.8, 25.79) * mm});
            skLineSegment(sketch, "E38.0.187", {"start": v(25.8, 25.79) * mm, "end": v(26.73, 26.72) * mm});
            skArc(sketch, "E38.0.188", {"start": v(26.73, 26.72) * mm, "mid": v(26.93, 26.96) * mm, "end": v(27.08, 27.25) * mm});
            skArc(sketch, "E38.0.189", {"start": v(27.08, 27.25) * mm, "mid": v(27.54, 28.75) * mm, "end": v(27.76, 30.31) * mm});
            skArc(sketch, "E38.0.190", {"start": v(27.76, 30.31) * mm, "mid": v(27.72, 30.52) * mm, "end": v(27.6, 30.7) * mm});
            skLineSegment(sketch, "E38.0.191", {"start": v(27.6, 30.7) * mm, "end": v(27.24, 31.06) * mm});
            skLineSegment(sketch, "E38.0.192", {"start": v(27.24, 31.06) * mm, "end": v(26.83, 31.38) * mm});
            skArc(sketch, "E38.0.193", {"start": v(26.83, 31.38) * mm, "mid": v(26.64, 31.47) * mm, "end": v(26.43, 31.48) * mm});
            skArc(sketch, "E38.0.194", {"start": v(26.43, 31.48) * mm, "mid": v(24.9, 31.06) * mm, "end": v(23.48, 30.4) * mm});
            skArc(sketch, "E38.0.195", {"start": v(23.48, 30.4) * mm, "mid": v(23.22, 30.22) * mm, "end": v(23, 29.99) * mm});
            skLineSegment(sketch, "E38.0.196", {"start": v(23, 29.99) * mm, "end": v(22.2, 28.94) * mm});
            skArc(sketch, "E38.0.197", {"start": v(22.2, 28.94) * mm, "mid": v(21.18, 28.34) * mm, "end": v(20.03, 28.61) * mm});
            skArc(sketch, "E38.0.198", {"start": v(20.03, 28.61) * mm, "mid": v(19.4, 29.04) * mm, "end": v(18.77, 29.45) * mm});
            skArc(sketch, "E38.0.199", {"start": v(18.77, 29.45) * mm, "mid": v(18.08, 30.42) * mm, "end": v(18.25, 31.59) * mm});
            skLineSegment(sketch, "E38.0.200", {"start": v(18.25, 31.59) * mm, "end": v(18.9, 32.72) * mm});
            skArc(sketch, "E38.0.201", {"start": v(18.9, 32.72) * mm, "mid": v(19.03, 33.01) * mm, "end": v(19.1, 33.33) * mm});
            skArc(sketch, "E38.0.202", {"start": v(19.1, 33.33) * mm, "mid": v(19.16, 34.9) * mm, "end": v(18.96, 36.46) * mm});
            skArc(sketch, "E38.0.203", {"start": v(18.96, 36.46) * mm, "mid": v(18.88, 36.66) * mm, "end": v(18.72, 36.8) * mm});
            skLineSegment(sketch, "E38.0.204", {"start": v(18.72, 36.8) * mm, "end": v(18.27, 37.06) * mm});
            skLineSegment(sketch, "E38.0.205", {"start": v(18.27, 37.06) * mm, "end": v(17.8, 37.25) * mm});
            skArc(sketch, "E38.0.206", {"start": v(17.8, 37.25) * mm, "mid": v(17.59, 37.3) * mm, "end": v(17.38, 37.24) * mm});
            skArc(sketch, "E38.0.207", {"start": v(17.38, 37.24) * mm, "mid": v(16.02, 36.45) * mm, "end": v(14.8, 35.44) * mm});
            skArc(sketch, "E38.0.208", {"start": v(14.8, 35.44) * mm, "mid": v(14.6, 35.2) * mm, "end": v(14.45, 34.92) * mm});
            skLineSegment(sketch, "E38.0.209", {"start": v(14.45, 34.92) * mm, "end": v(13.95, 33.7) * mm});
            skArc(sketch, "E38.0.210", {"start": v(13.95, 33.7) * mm, "mid": v(13.12, 32.86) * mm, "end": v(11.94, 32.82) * mm});
            skArc(sketch, "E38.0.211", {"start": v(11.94, 32.82) * mm, "mid": v(11.23, 33.07) * mm, "end": v(10.5, 33.3) * mm});
            skArc(sketch, "E38.0.212", {"start": v(10.5, 33.3) * mm, "mid": v(9.6, 34.06) * mm, "end": v(9.45, 35.23) * mm});
            skLineSegment(sketch, "E38.0.213", {"start": v(9.45, 35.23) * mm, "end": v(9.79, 36.5) * mm});
            skArc(sketch, "E38.0.214", {"start": v(9.79, 36.5) * mm, "mid": v(9.84, 36.82) * mm, "end": v(9.83, 37.13) * mm});
            skArc(sketch, "E38.0.215", {"start": v(9.83, 37.13) * mm, "mid": v(9.48, 38.67) * mm, "end": v(8.88, 40.13) * mm});
            skArc(sketch, "E38.0.216", {"start": v(8.88, 40.13) * mm, "mid": v(8.75, 40.3) * mm, "end": v(8.56, 40.39) * mm});
            skLineSegment(sketch, "E38.0.217", {"start": v(8.56, 40.39) * mm, "end": v(8.06, 40.52) * mm});
            skLineSegment(sketch, "E38.0.218", {"start": v(8.06, 40.52) * mm, "end": v(7.55, 40.6) * mm});
            skArc(sketch, "E38.0.219", {"start": v(7.55, 40.6) * mm, "mid": v(7.34, 40.57) * mm, "end": v(7.15, 40.47) * mm});
            skArc(sketch, "E38.0.220", {"start": v(7.15, 40.47) * mm, "mid": v(6.04, 39.36) * mm, "end": v(5.13, 38.07) * mm});
            skArc(sketch, "E38.0.221", {"start": v(5.13, 38.07) * mm, "mid": v(5, 37.78) * mm, "end": v(4.92, 37.47) * mm});
            skLineSegment(sketch, "E38.0.222", {"start": v(4.92, 37.47) * mm, "end": v(4.75, 36.17) * mm});
            skArc(sketch, "E38.0.223", {"start": v(4.75, 36.17) * mm, "mid": v(4.17, 35.14) * mm, "end": v(3.04, 34.8) * mm});
            skArc(sketch, "E38.0.224", {"start": v(3.04, 34.8) * mm, "mid": v(2.28, 34.85) * mm, "end": v(1.53, 34.9) * mm});
            skArc(sketch, "E38.0.225", {"start": v(1.53, 34.9) * mm, "mid": v(0.45, 35.38) * mm, "end": v(0, 36.48) * mm});
            skLineSegment(sketch, "E38.0.226", {"start": v(0, 36.48) * mm, "end": v(0, 37.8) * mm});
            skArc(sketch, "E38.0.227", {"start": v(0, 37.8) * mm, "mid": v(-0.02, 38.1) * mm, "end": v(-0.12, 38.41) * mm});
            skArc(sketch, "E38.0.228", {"start": v(-0.12, 38.41) * mm, "mid": v(-0.85, 39.8) * mm, "end": v(-1.8, 41.06) * mm});
            skArc(sketch, "E38.0.229", {"start": v(-1.8, 41.06) * mm, "mid": v(-1.98, 41.18) * mm, "end": v(-2.18, 41.23) * mm});
            skLineSegment(sketch, "E38.0.230", {"start": v(-2.18, 41.23) * mm, "end": v(-2.7, 41.23) * mm});
            skLineSegment(sketch, "E38.0.231", {"start": v(-2.7, 41.23) * mm, "end": v(-3.22, 41.16) * mm});
            skArc(sketch, "E38.0.232", {"start": v(-3.22, 41.16) * mm, "mid": v(-3.41, 41.1) * mm, "end": v(-3.57, 40.95) * mm});
            skArc(sketch, "E38.0.233", {"start": v(-3.57, 40.95) * mm, "mid": v(-4.35, 39.58) * mm, "end": v(-4.9, 38.1) * mm});
            skArc(sketch, "E38.0.234", {"start": v(-4.9, 38.1) * mm, "mid": v(-4.95, 37.79) * mm, "end": v(-4.94, 37.47) * mm});
            skLineSegment(sketch, "E38.0.235", {"start": v(-4.94, 37.47) * mm, "end": v(-4.77, 36.16) * mm});
            skArc(sketch, "E38.0.236", {"start": v(-4.77, 36.16) * mm, "mid": v(-5.06, 35.02) * mm, "end": v(-6.07, 34.4) * mm});
            skArc(sketch, "E38.0.237", {"start": v(-6.07, 34.4) * mm, "mid": v(-6.81, 34.25) * mm, "end": v(-7.56, 34.1) * mm});
            skArc(sketch, "E38.0.238", {"start": v(-7.56, 34.1) * mm, "mid": v(-8.72, 34.3) * mm, "end": v(-9.43, 35.24) * mm});
            skLineSegment(sketch, "E38.0.239", {"start": v(-9.43, 35.24) * mm, "end": v(-9.77, 36.5) * mm});
            skArc(sketch, "E38.0.240", {"start": v(-9.77, 36.5) * mm, "mid": v(-9.89, 36.8) * mm, "end": v(-10.06, 37.07) * mm});
            skArc(sketch, "E38.0.241", {"start": v(-10.06, 37.07) * mm, "mid": v(-11.13, 38.23) * mm, "end": v(-12.37, 39.2) * mm});
            skArc(sketch, "E38.0.242", {"start": v(-12.37, 39.2) * mm, "mid": v(-12.57, 39.27) * mm, "end": v(-12.78, 39.26) * mm});
            skLineSegment(sketch, "E38.0.243", {"start": v(-12.78, 39.26) * mm, "end": v(-13.28, 39.12) * mm});
            skLineSegment(sketch, "E38.0.244", {"start": v(-13.28, 39.12) * mm, "end": v(-13.76, 38.93) * mm});
            skArc(sketch, "E38.0.245", {"start": v(-13.76, 38.93) * mm, "mid": v(-13.93, 38.8) * mm, "end": v(-14.04, 38.63) * mm});
            skArc(sketch, "E38.0.246", {"start": v(-14.04, 38.63) * mm, "mid": v(-14.45, 37.1) * mm, "end": v(-14.6, 35.53) * mm});
            skArc(sketch, "E38.0.247", {"start": v(-14.6, 35.53) * mm, "mid": v(-14.56, 35.22) * mm, "end": v(-14.47, 34.91) * mm});
            skLineSegment(sketch, "E38.0.248", {"start": v(-14.47, 34.91) * mm, "end": v(-13.97, 33.7) * mm});
            skArc(sketch, "E38.0.249", {"start": v(-13.97, 33.7) * mm, "mid": v(-13.95, 32.51) * mm, "end": v(-14.76, 31.65) * mm});
            skArc(sketch, "E38.0.250", {"start": v(-14.76, 31.65) * mm, "mid": v(-15.45, 31.32) * mm, "end": v(-16.12, 30.98) * mm});
            skArc(sketch, "E38.0.251", {"start": v(-16.12, 30.98) * mm, "mid": v(-17.3, 30.86) * mm, "end": v(-18.23, 31.6) * mm});
            skLineSegment(sketch, "E38.0.252", {"start": v(-18.23, 31.6) * mm, "end": v(-18.89, 32.73) * mm});
            skArc(sketch, "E38.0.253", {"start": v(-18.89, 32.73) * mm, "mid": v(-19.07, 33) * mm, "end": v(-19.3, 33.2) * mm});
            skArc(sketch, "E38.0.254", {"start": v(-19.3, 33.2) * mm, "mid": v(-20.64, 34.05) * mm, "end": v(-22.1, 34.66) * mm});
            skArc(sketch, "E38.0.255", {"start": v(-22.1, 34.66) * mm, "mid": v(-22.3, 34.68) * mm, "end": v(-22.5, 34.61) * mm});
            skLineSegment(sketch, "E38.0.256", {"start": v(-22.5, 34.61) * mm, "end": v(-22.95, 34.35) * mm});
            skLineSegment(sketch, "E38.0.257", {"start": v(-22.95, 34.35) * mm, "end": v(-23.36, 34.04) * mm});
            skArc(sketch, "E38.0.258", {"start": v(-23.36, 34.04) * mm, "mid": v(-23.5, 33.88) * mm, "end": v(-23.56, 33.68) * mm});
            skArc(sketch, "E38.0.259", {"start": v(-23.56, 33.68) * mm, "mid": v(-23.56, 32.1) * mm, "end": v(-23.3, 30.55) * mm});
            skArc(sketch, "E38.0.260", {"start": v(-23.3, 30.55) * mm, "mid": v(-23.18, 30.25) * mm, "end": v(-23.01, 29.98) * mm});
            skLineSegment(sketch, "E38.0.261", {"start": v(-23.01, 29.98) * mm, "end": v(-22.21, 28.93) * mm});
            skArc(sketch, "E38.0.262", {"start": v(-22.21, 28.93) * mm, "mid": v(-21.9, 27.8) * mm, "end": v(-22.45, 26.75) * mm});
            skArc(sketch, "E38.0.263", {"start": v(-22.45, 26.75) * mm, "mid": v(-23.03, 26.26) * mm, "end": v(-23.6, 25.75) * mm});
            skArc(sketch, "E38.0.264", {"start": v(-23.6, 25.75) * mm, "mid": v(-24.7, 25.34) * mm, "end": v(-25.79, 25.8) * mm});
            skLineSegment(sketch, "E38.0.265", {"start": v(-25.79, 25.8) * mm, "end": v(-26.72, 26.73) * mm});
            skArc(sketch, "E38.0.266", {"start": v(-26.72, 26.73) * mm, "mid": v(-26.96, 26.93) * mm, "end": v(-27.25, 27.08) * mm});
            skArc(sketch, "E38.0.267", {"start": v(-27.25, 27.08) * mm, "mid": v(-28.75, 27.54) * mm, "end": v(-30.31, 27.76) * mm});
            skArc(sketch, "E38.0.268", {"start": v(-30.31, 27.76) * mm, "mid": v(-30.52, 27.72) * mm, "end": v(-30.7, 27.6) * mm});
            skLineSegment(sketch, "E38.0.269", {"start": v(-30.7, 27.6) * mm, "end": v(-31.06, 27.24) * mm});
            skLineSegment(sketch, "E38.0.270", {"start": v(-31.06, 27.24) * mm, "end": v(-31.38, 26.83) * mm});
            skArc(sketch, "E38.0.271", {"start": v(-31.38, 26.83) * mm, "mid": v(-31.47, 26.64) * mm, "end": v(-31.48, 26.43) * mm});
            skArc(sketch, "E38.0.272", {"start": v(-31.48, 26.43) * mm, "mid": v(-31.06, 24.9) * mm, "end": v(-30.4, 23.48) * mm});
            skArc(sketch, "E38.0.273", {"start": v(-30.4, 23.48) * mm, "mid": v(-30.22, 23.22) * mm, "end": v(-29.99, 23) * mm});
            skLineSegment(sketch, "E38.0.274", {"start": v(-29.99, 23) * mm, "end": v(-28.94, 22.2) * mm});
            skArc(sketch, "E38.0.275", {"start": v(-28.94, 22.2) * mm, "mid": v(-28.34, 21.18) * mm, "end": v(-28.61, 20.03) * mm});
            skArc(sketch, "E38.0.276", {"start": v(-28.61, 20.03) * mm, "mid": v(-29.04, 19.4) * mm, "end": v(-29.45, 18.77) * mm});
            skArc(sketch, "E38.0.277", {"start": v(-29.45, 18.77) * mm, "mid": v(-30.42, 18.08) * mm, "end": v(-31.59, 18.25) * mm});
            skLineSegment(sketch, "E38.0.278", {"start": v(-31.59, 18.25) * mm, "end": v(-32.72, 18.9) * mm});
            skArc(sketch, "E38.0.279", {"start": v(-32.72, 18.9) * mm, "mid": v(-33.01, 19.03) * mm, "end": v(-33.33, 19.1) * mm});
            skArc(sketch, "E38.0.280", {"start": v(-33.33, 19.1) * mm, "mid": v(-34.9, 19.16) * mm, "end": v(-36.46, 18.96) * mm});
            skArc(sketch, "E38.0.281", {"start": v(-36.46, 18.96) * mm, "mid": v(-36.66, 18.88) * mm, "end": v(-36.8, 18.72) * mm});
            skLineSegment(sketch, "E38.0.282", {"start": v(-36.8, 18.72) * mm, "end": v(-37.06, 18.27) * mm});
            skLineSegment(sketch, "E38.0.283", {"start": v(-37.06, 18.27) * mm, "end": v(-37.25, 17.8) * mm});
            skArc(sketch, "E38.0.284", {"start": v(-37.25, 17.8) * mm, "mid": v(-37.3, 17.59) * mm, "end": v(-37.24, 17.38) * mm});
            skArc(sketch, "E38.0.285", {"start": v(-37.24, 17.38) * mm, "mid": v(-36.45, 16.02) * mm, "end": v(-35.44, 14.8) * mm});
            skArc(sketch, "E38.0.286", {"start": v(-35.44, 14.8) * mm, "mid": v(-35.2, 14.6) * mm, "end": v(-34.92, 14.45) * mm});
            skLineSegment(sketch, "E38.0.287", {"start": v(-34.92, 14.45) * mm, "end": v(-33.7, 13.95) * mm});
            skArc(sketch, "E38.0.288", {"start": v(-33.7, 13.95) * mm, "mid": v(-32.86, 13.12) * mm, "end": v(-32.82, 11.94) * mm});
            skArc(sketch, "E38.0.289", {"start": v(-32.82, 11.94) * mm, "mid": v(-33.07, 11.23) * mm, "end": v(-33.3, 10.5) * mm});
            skArc(sketch, "E38.0.290", {"start": v(-33.3, 10.5) * mm, "mid": v(-34.06, 9.6) * mm, "end": v(-35.23, 9.45) * mm});
            skLineSegment(sketch, "E38.0.291", {"start": v(-35.23, 9.45) * mm, "end": v(-36.5, 9.79) * mm});
            skArc(sketch, "E38.0.292", {"start": v(-36.5, 9.79) * mm, "mid": v(-36.82, 9.84) * mm, "end": v(-37.13, 9.83) * mm});
            skArc(sketch, "E38.0.293", {"start": v(-37.13, 9.83) * mm, "mid": v(-38.67, 9.48) * mm, "end": v(-40.13, 8.88) * mm});
            skArc(sketch, "E38.0.294", {"start": v(-40.13, 8.88) * mm, "mid": v(-40.3, 8.75) * mm, "end": v(-40.39, 8.56) * mm});
            skLineSegment(sketch, "E38.0.295", {"start": v(-40.39, 8.56) * mm, "end": v(-40.52, 8.06) * mm});
            skLineSegment(sketch, "E38.0.296", {"start": v(-40.52, 8.06) * mm, "end": v(-40.6, 7.55) * mm});
            skArc(sketch, "E38.0.297", {"start": v(-40.6, 7.55) * mm, "mid": v(-40.57, 7.34) * mm, "end": v(-40.47, 7.15) * mm});
            skArc(sketch, "E38.0.298", {"start": v(-40.47, 7.15) * mm, "mid": v(-39.36, 6.04) * mm, "end": v(-38.07, 5.13) * mm});
            skArc(sketch, "E38.0.299", {"start": v(-38.07, 5.13) * mm, "mid": v(-37.78, 5) * mm, "end": v(-37.47, 4.92) * mm});
            skLineSegment(sketch, "E38.0.300", {"start": v(-37.47, 4.92) * mm, "end": v(-36.17, 4.75) * mm});
            skArc(sketch, "E38.0.301", {"start": v(-36.17, 4.75) * mm, "mid": v(-35.14, 4.17) * mm, "end": v(-34.8, 3.04) * mm});
            skArc(sketch, "E38.0.302", {"start": v(-34.8, 3.04) * mm, "mid": v(-34.85, 2.28) * mm, "end": v(-34.9, 1.53) * mm});
            skArc(sketch, "E38.0.303", {"start": v(-34.9, 1.53) * mm, "mid": v(-35.38, 0.45) * mm, "end": v(-36.48, 0) * mm});
            skLineSegment(sketch, "E38.0.304", {"start": v(-36.48, 0) * mm, "end": v(-37.8, 0) * mm});
            skArc(sketch, "E38.0.305", {"start": v(-37.8, 0) * mm, "mid": v(-38.1, -0.02) * mm, "end": v(-38.41, -0.12) * mm});
            skArc(sketch, "E38.0.306", {"start": v(-38.41, -0.12) * mm, "mid": v(-39.8, -0.85) * mm, "end": v(-41.06, -1.8) * mm});
            skArc(sketch, "E38.0.307", {"start": v(-41.06, -1.8) * mm, "mid": v(-41.18, -1.98) * mm, "end": v(-41.23, -2.18) * mm});
            skLineSegment(sketch, "E38.0.308", {"start": v(-41.23, -2.18) * mm, "end": v(-41.23, -2.7) * mm});
            skLineSegment(sketch, "E38.0.309", {"start": v(-41.23, -2.7) * mm, "end": v(-41.16, -3.22) * mm});
            skArc(sketch, "E38.0.310", {"start": v(-41.16, -3.22) * mm, "mid": v(-41.1, -3.41) * mm, "end": v(-40.95, -3.57) * mm});
            skArc(sketch, "E38.0.311", {"start": v(-40.95, -3.57) * mm, "mid": v(-39.58, -4.35) * mm, "end": v(-38.1, -4.9) * mm});
            skSolve(sketch);
        }
        {
            var Q0;
            Q0=makeQuery(id+"F0.imprint","IMPRINT",FACE,{"disambiguationData":[TD([[makeQuery(id+"F0.imprint","IMPRINT",EDGE,{"derivedFrom":sQuery(id+"F0.wireOp",EDGE,"E0")}),1.0]])]});
            var Q1;
            Q1=makeQuery(id+"F2.imprint","IMPRINT",FACE,{"disambiguationData":[TD([[makeQuery(id+"F2.imprint","IMPRINT",EDGE,{"derivedFrom":sQuery(id+"F2.wireOp",EDGE,"E38.0.0")}),1.0]])]});
            var Q2;
            Q2=sQuery(id+"F0.wireOp",VERTEX,"E14.18.23.0.start");
            var Q3;
            Q3=sQuery(id+"F2.wireOp",VERTEX,"E38.0.234.start");
            loft(context, id + "F3", {"sheetProfilesArray" : [{ "sheetProfileEntities" : qUnion([Q0]) }, { "sheetProfileEntities" : qUnion([Q1]) }], "matchConnections" : true, "connections" : [{ "connectionEntities" : qUnion([Q2, Q3]), "connectionEdgeQueries" : qUnion([]), "connectionEdgeParameters" : [] }]});
        }
        {
            var Q0;
            Q0=makeQuery(id+"F3.opLoft","CAP_FACE",FACE,{"disambiguationData":[OSD([makeQuery(id+"F2.imprint","IMPRINT",FACE,{"disambiguationData":[TD([[makeQuery(id+"F2.imprint","IMPRINT",EDGE,{"derivedFrom":sQuery(id+"F2.wireOp",EDGE,"E38.0.0")}),1.0]])]})])],"isStart":true});
            var sketch = newSketch(context, id + "F4", { "sketchPlane" : qUnion([Q0])});
            skPoint(sketch, "E39", {"position": v(0, 0) * mm});
            skSolve(sketch);
        }
        {
            var Q0;
            Q0=sQuery(id+"F4.wireOp",VERTEX,"E39");
            var Q1;
            Q1=makeQuery(id+"F3.opLoft","SWEPT_BODY",BODY,{"disambiguationData":[OSD([makeQuery(id+"F0.imprint","IMPRINT",FACE,{"disambiguationData":[TD([[makeQuery(id+"F0.imprint","IMPRINT",EDGE,{"derivedFrom":sQuery(id+"F0.wireOp",EDGE,"E0")}),1.0]])]}),makeQuery(id+"F2.imprint","IMPRINT",FACE,{"disambiguationData":[TD([[makeQuery(id+"F2.imprint","IMPRINT",EDGE,{"derivedFrom":sQuery(id+"F2.wireOp",EDGE,"E38.0.0")}),1.0]])]})])]});
            hole(context, id + "F5", {"style" : HoleStyle.SIMPLE, "endStyle" : HoleEndStyle.THROUGH, "holeDiameter" : 12.7 * mm, "tappedDepth" : 12.7 * mm, "tapClearance" : 3, "locations" : qUnion([Q0]), "scope" : qUnion([Q1])});
        }
    });
